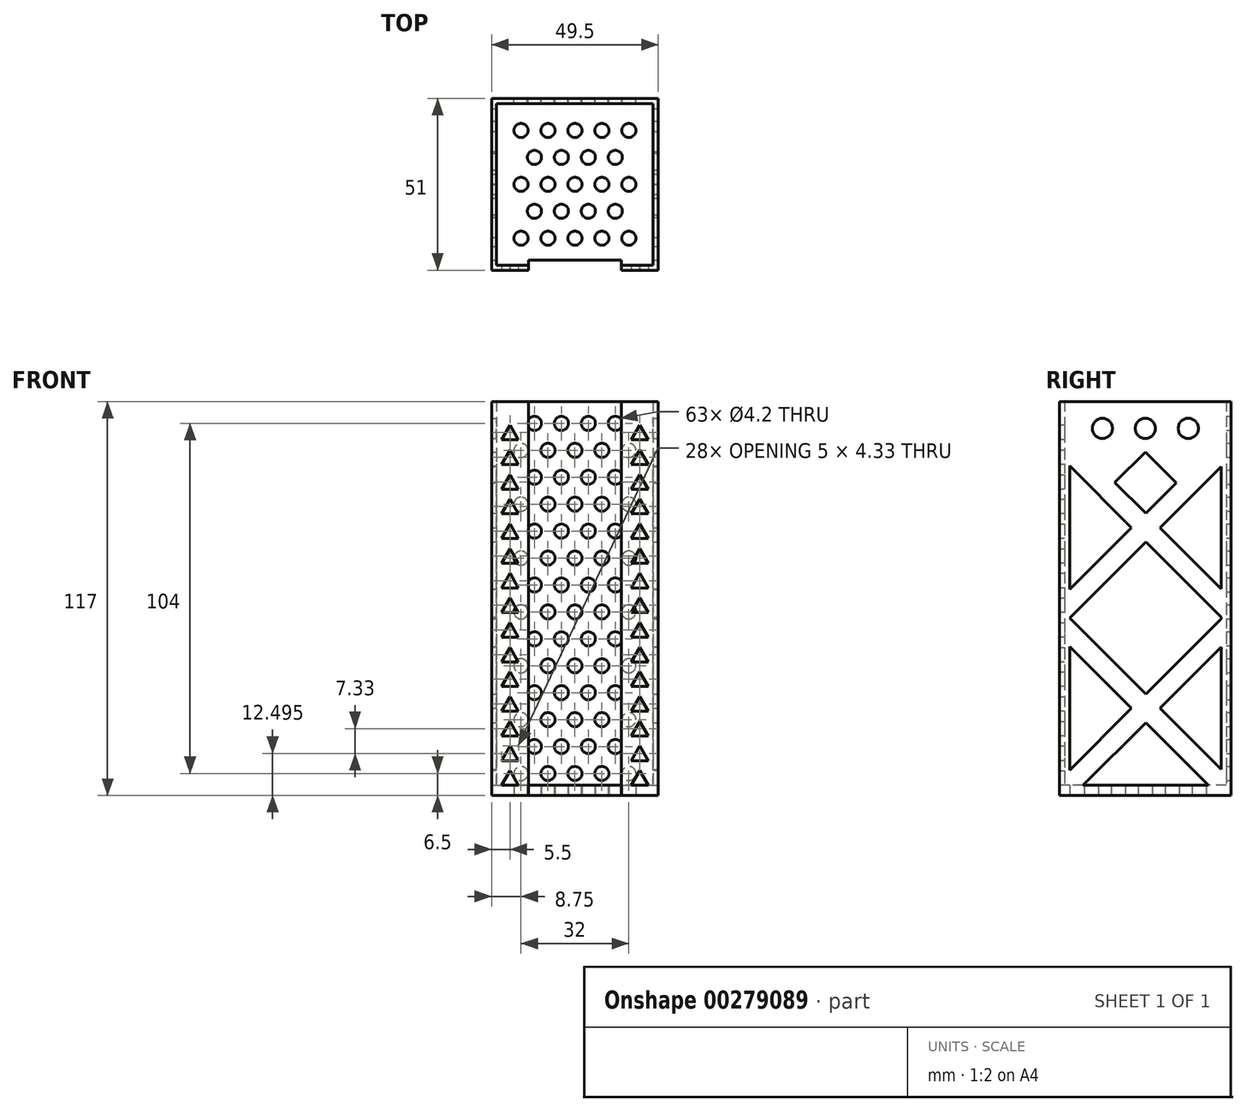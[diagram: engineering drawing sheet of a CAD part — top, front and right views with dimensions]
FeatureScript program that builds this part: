
annotation { "Feature Type Name" : "Feature", "Feature Type Description" : "" }
export const myFeature = defineFeature(function(context is Context, id is Id, definition is map)
    precondition{}
    {
        {
            var Q0;
            Q0=qCreatedBy(makeId("Top.planeOp"),FACE);
            var sketch = newSketch(context, id + "F0", { "sketchPlane" : qUnion([Q0])});
            skLineSegment(sketch, "E0.bottom", {"start": v(-24.75, 25.5) * mm, "end": v(24.75, 25.5) * mm});
            skLineSegment(sketch, "E0.top", {"start": v(-24.75, -25.5) * mm, "end": v(24.75, -25.5) * mm});
            skLineSegment(sketch, "E0.left", {"start": v(-24.75, 25.5) * mm, "end": v(-24.75, -25.5) * mm});
            skLineSegment(sketch, "E0.right", {"start": v(24.75, 25.5) * mm, "end": v(24.75, -25.5) * mm});
            skPoint(sketch, "E0.middle", {"position": v(0, 0) * mm});
            skSolve(sketch);
        }
        {
            var Q0;
            Q0=makeQuery(id+"F0.imprint","IMPRINT",FACE,{"disambiguationData":[TD([[makeQuery(id+"F0.imprint","IMPRINT",EDGE,{"derivedFrom":sQuery(id+"F0.wireOp",EDGE,"E0.bottom")}),-1.0]])]});
            extrude(context, id + "F1", {"entities" : qUnion([Q0]), "depth" : 3 * mm});
        }
        {
            var Q0;
            Q0=makeQuery(id+"F1.opExtrude","CAP_FACE",FACE,{"disambiguationData":[OSD([sQuery(id+"F0.wireOp",EDGE,"E0.bottom"),sQuery(id+"F0.wireOp",EDGE,"E0.top"),sQuery(id+"F0.wireOp",EDGE,"E0.left"),sQuery(id+"F0.wireOp",EDGE,"E0.right")])],"isStart":false});
            var sketch = newSketch(context, id + "F2", { "sketchPlane" : qUnion([Q0])});
            skLineSegment(sketch, "E1.bottom", {"start": v(-23.25, 24) * mm, "end": v(23.25, 24) * mm});
            skLineSegment(sketch, "E1.top", {"start": v(-23.25, -24) * mm, "end": v(23.25, -24) * mm});
            skLineSegment(sketch, "E1.left", {"start": v(-23.25, 24) * mm, "end": v(-23.25, -24) * mm});
            skLineSegment(sketch, "E1.right", {"start": v(23.25, 24) * mm, "end": v(23.25, -24) * mm});
            skPoint(sketch, "E1.middle", {"position": v(0, 0) * mm});
            skLineSegment(sketch, "E2.bottom", {"start": v(-24.75, 25.5) * mm, "end": v(24.75, 25.5) * mm});
            skLineSegment(sketch, "E2.top", {"start": v(-24.75, -25.5) * mm, "end": v(24.75, -25.5) * mm});
            skLineSegment(sketch, "E2.left", {"start": v(-24.75, 25.5) * mm, "end": v(-24.75, -25.5) * mm});
            skLineSegment(sketch, "E2.right", {"start": v(24.75, 25.5) * mm, "end": v(24.75, -25.5) * mm});
            skSolve(sketch);
        }
        {
            var Q0;
            Q0 = qSketchRegion(id + "F2", true);
            extrude(context, id + "F3", {"entities" : qUnion([Q0]), "operationType" : NewBodyOperationType.ADD, "depth" : 114 * mm});
        }
        {
            var Q0;
            Q0=makeQuery(id+"F3.boolean.opBoolean","MERGE",FACE,{"derivedFrom":[makeQuery(id+"F1.opExtrude","SWEPT_FACE",FACE,{"disambiguationData":[OSD([sQuery(id+"F0.wireOp",EDGE,"E0.top")])]}),makeQuery(id+"F3.opExtrude","SWEPT_FACE",FACE,{"disambiguationData":[OSD([sQuery(id+"F2.wireOp",EDGE,"E2.top")])]})]});
            var sketch = newSketch(context, id + "F4", { "sketchPlane" : qUnion([Q0])});
            skLineSegment(sketch, "E3.bottom", {"start": v(-24.75, 117) * mm, "end": v(-13.75, 117) * mm});
            skLineSegment(sketch, "E3.top", {"start": v(-24.75, 0) * mm, "end": v(-13.75, 0) * mm});
            skLineSegment(sketch, "E3.left", {"start": v(-24.75, 117) * mm, "end": v(-24.75, 0) * mm});
            skLineSegment(sketch, "E3.right", {"start": v(-13.75, 117) * mm, "end": v(-13.75, 0) * mm});
            skLineSegment(sketch, "E4.bottom", {"start": v(24.75, 117) * mm, "end": v(13.75, 117) * mm});
            skLineSegment(sketch, "E4.top", {"start": v(24.75, 0) * mm, "end": v(13.75, 0) * mm});
            skLineSegment(sketch, "E4.left", {"start": v(24.75, 117) * mm, "end": v(24.75, 0) * mm});
            skLineSegment(sketch, "E4.right", {"start": v(13.75, 117) * mm, "end": v(13.75, 0) * mm});
            skLineSegment(sketch, "E5.bottom", {"start": v(-13.75, 117) * mm, "end": v(13.75, 117) * mm});
            skLineSegment(sketch, "E5.top", {"start": v(-13.75, 0) * mm, "end": v(13.75, 0) * mm});
            skSolve(sketch);
        }
        {
            var Q0;
            Q0=makeQuery(id+"F4.imprint","IMPRINT",FACE,{"disambiguationData":[TD([[makeQuery(id+"F4.imprint","IMPRINT",EDGE,{"derivedFrom":sQuery(id+"F4.wireOp",EDGE,"E5.bottom")}),-1.0]])]});
            extrude(context, id + "F5", {"entities" : qUnion([Q0]), "operationType" : NewBodyOperationType.REMOVE, "oppositeDirection" : true, "depth" : 3 * mm});
        }
        {
            var Q0;
            Q0=makeQuery(id+"F3.boolean.opBoolean","MERGE",FACE,{"derivedFrom":[makeQuery(id+"F1.opExtrude","SWEPT_FACE",FACE,{"disambiguationData":[OSD([sQuery(id+"F0.wireOp",EDGE,"E0.bottom")])]}),makeQuery(id+"F3.opExtrude","SWEPT_FACE",FACE,{"disambiguationData":[OSD([sQuery(id+"F2.wireOp",EDGE,"E2.bottom")])]})]});
            var sketch = newSketch(context, id + "F6", { "sketchPlane" : qUnion([Q0])});
            skPoint(sketch, "E6.endSnap0", {"position": v(0, 0) * mm});
            skLineSegment(sketch, "E7", {"start": v(0, 6.5) * mm, "end": v(-8, 6.5) * mm});
            skLineSegment(sketch, "E8", {"start": v(-8, 6.5) * mm, "end": v(-16, 6.5) * mm});
            skLineSegment(sketch, "E9", {"start": v(0, 6.5) * mm, "end": v(8, 6.5) * mm});
            skLineSegment(sketch, "E10", {"start": v(8, 6.5) * mm, "end": v(16, 6.5) * mm});
            skCircle(sketch, "E11", {"center": v(-16, 6.5) * mm, "radius": 2.1 * mm});
            skCircle(sketch, "E12", {"center": v(-8, 6.5) * mm, "radius": 2.1 * mm});
            skCircle(sketch, "E13", {"center": v(0, 6.5) * mm, "radius": 2.1 * mm});
            skCircle(sketch, "E14", {"center": v(8, 6.5) * mm, "radius": 2.1 * mm});
            skCircle(sketch, "E15", {"center": v(16, 6.5) * mm, "radius": 2.1 * mm});
            skLineSegment(sketch, "E16", {"start": v(-12, 6.5) * mm, "end": v(-12, 14.5) * mm});
            skLineSegment(sketch, "E17", {"start": v(-4, 6.5) * mm, "end": v(-4, 14.5) * mm});
            skLineSegment(sketch, "E18", {"start": v(4, 6.5) * mm, "end": v(4, 14.5) * mm});
            skLineSegment(sketch, "E19", {"start": v(12, 6.5) * mm, "end": v(12, 14.5) * mm});
            skCircle(sketch, "E20", {"center": v(-12, 14.5) * mm, "radius": 2.1 * mm});
            skCircle(sketch, "E21", {"center": v(-4, 14.5) * mm, "radius": 2.1 * mm});
            skCircle(sketch, "E22", {"center": v(4, 14.5) * mm, "radius": 2.1 * mm});
            skCircle(sketch, "E23", {"center": v(12, 14.5) * mm, "radius": 2.1 * mm});
            skCircle(sketch, "E24.0.1.0", {"center": v(12, 30.5) * mm, "radius": 2.1 * mm});
            skLineSegment(sketch, "E24.0.1.1", {"start": v(12, 22.5) * mm, "end": v(12, 30.5) * mm});
            skCircle(sketch, "E24.0.1.2", {"center": v(-4, 30.5) * mm, "radius": 2.1 * mm});
            skCircle(sketch, "E24.0.1.3", {"center": v(-12, 30.5) * mm, "radius": 2.1 * mm});
            skLineSegment(sketch, "E24.0.1.4", {"start": v(0, 14.5) * mm, "end": v(0, 22.5) * mm});
            skPoint(sketch, "E24.0.1.5", {"position": v(0, 16) * mm});
            skLineSegment(sketch, "E24.0.1.6", {"start": v(-8, 22.5) * mm, "end": v(-16, 22.5) * mm});
            skLineSegment(sketch, "E24.0.1.7", {"start": v(0, 22.5) * mm, "end": v(8, 22.5) * mm});
            skCircle(sketch, "E24.0.1.8", {"center": v(-16, 22.5) * mm, "radius": 2.1 * mm});
            skCircle(sketch, "E24.0.1.9", {"center": v(-8, 22.5) * mm, "radius": 2.1 * mm});
            skCircle(sketch, "E24.0.1.10", {"center": v(0, 22.5) * mm, "radius": 2.1 * mm});
            skLineSegment(sketch, "E24.0.1.11", {"start": v(4, 22.5) * mm, "end": v(4, 30.5) * mm});
            skLineSegment(sketch, "E24.0.1.12", {"start": v(-4, 22.5) * mm, "end": v(-4, 30.5) * mm});
            skLineSegment(sketch, "E24.0.1.13", {"start": v(-12, 22.5) * mm, "end": v(-12, 30.5) * mm});
            skCircle(sketch, "E24.0.1.14", {"center": v(4, 30.5) * mm, "radius": 2.1 * mm});
            skCircle(sketch, "E24.0.1.15", {"center": v(16, 22.5) * mm, "radius": 2.1 * mm});
            skCircle(sketch, "E24.0.1.16", {"center": v(8, 22.5) * mm, "radius": 2.1 * mm});
            skLineSegment(sketch, "E24.0.1.17", {"start": v(0, 22.5) * mm, "end": v(-8, 22.5) * mm});
            skLineSegment(sketch, "E24.0.1.18", {"start": v(8, 22.5) * mm, "end": v(16, 22.5) * mm});
            skCircle(sketch, "E24.0.2.0", {"center": v(12, 46.5) * mm, "radius": 2.1 * mm});
            skLineSegment(sketch, "E24.0.2.1", {"start": v(12, 38.5) * mm, "end": v(12, 46.5) * mm});
            skCircle(sketch, "E24.0.2.2", {"center": v(-4, 46.5) * mm, "radius": 2.1 * mm});
            skCircle(sketch, "E24.0.2.3", {"center": v(-12, 46.5) * mm, "radius": 2.1 * mm});
            skLineSegment(sketch, "E24.0.2.4", {"start": v(0, 30.5) * mm, "end": v(0, 38.5) * mm});
            skPoint(sketch, "E24.0.2.5", {"position": v(0, 32) * mm});
            skLineSegment(sketch, "E24.0.2.6", {"start": v(-8, 38.5) * mm, "end": v(-16, 38.5) * mm});
            skLineSegment(sketch, "E24.0.2.7", {"start": v(0, 38.5) * mm, "end": v(8, 38.5) * mm});
            skCircle(sketch, "E24.0.2.8", {"center": v(-16, 38.5) * mm, "radius": 2.1 * mm});
            skCircle(sketch, "E24.0.2.9", {"center": v(-8, 38.5) * mm, "radius": 2.1 * mm});
            skCircle(sketch, "E24.0.2.10", {"center": v(0, 38.5) * mm, "radius": 2.1 * mm});
            skLineSegment(sketch, "E24.0.2.11", {"start": v(4, 38.5) * mm, "end": v(4, 46.5) * mm});
            skLineSegment(sketch, "E24.0.2.12", {"start": v(-4, 38.5) * mm, "end": v(-4, 46.5) * mm});
            skLineSegment(sketch, "E24.0.2.13", {"start": v(-12, 38.5) * mm, "end": v(-12, 46.5) * mm});
            skCircle(sketch, "E24.0.2.14", {"center": v(4, 46.5) * mm, "radius": 2.1 * mm});
            skCircle(sketch, "E24.0.2.15", {"center": v(16, 38.5) * mm, "radius": 2.1 * mm});
            skCircle(sketch, "E24.0.2.16", {"center": v(8, 38.5) * mm, "radius": 2.1 * mm});
            skLineSegment(sketch, "E24.0.2.17", {"start": v(0, 38.5) * mm, "end": v(-8, 38.5) * mm});
            skLineSegment(sketch, "E24.0.2.18", {"start": v(8, 38.5) * mm, "end": v(16, 38.5) * mm});
            skCircle(sketch, "E24.0.3.0", {"center": v(12, 62.5) * mm, "radius": 2.1 * mm});
            skLineSegment(sketch, "E24.0.3.1", {"start": v(12, 54.5) * mm, "end": v(12, 62.5) * mm});
            skCircle(sketch, "E24.0.3.2", {"center": v(-4, 62.5) * mm, "radius": 2.1 * mm});
            skCircle(sketch, "E24.0.3.3", {"center": v(-12, 62.5) * mm, "radius": 2.1 * mm});
            skLineSegment(sketch, "E24.0.3.4", {"start": v(0, 46.5) * mm, "end": v(0, 54.5) * mm});
            skPoint(sketch, "E24.0.3.5", {"position": v(0, 48) * mm});
            skLineSegment(sketch, "E24.0.3.6", {"start": v(-8, 54.5) * mm, "end": v(-16, 54.5) * mm});
            skLineSegment(sketch, "E24.0.3.7", {"start": v(0, 54.5) * mm, "end": v(8, 54.5) * mm});
            skCircle(sketch, "E24.0.3.8", {"center": v(-16, 54.5) * mm, "radius": 2.1 * mm});
            skCircle(sketch, "E24.0.3.9", {"center": v(-8, 54.5) * mm, "radius": 2.1 * mm});
            skCircle(sketch, "E24.0.3.10", {"center": v(0, 54.5) * mm, "radius": 2.1 * mm});
            skLineSegment(sketch, "E24.0.3.11", {"start": v(4, 54.5) * mm, "end": v(4, 62.5) * mm});
            skLineSegment(sketch, "E24.0.3.12", {"start": v(-4, 54.5) * mm, "end": v(-4, 62.5) * mm});
            skLineSegment(sketch, "E24.0.3.13", {"start": v(-12, 54.5) * mm, "end": v(-12, 62.5) * mm});
            skCircle(sketch, "E24.0.3.14", {"center": v(4, 62.5) * mm, "radius": 2.1 * mm});
            skCircle(sketch, "E24.0.3.15", {"center": v(16, 54.5) * mm, "radius": 2.1 * mm});
            skCircle(sketch, "E24.0.3.16", {"center": v(8, 54.5) * mm, "radius": 2.1 * mm});
            skLineSegment(sketch, "E24.0.3.17", {"start": v(0, 54.5) * mm, "end": v(-8, 54.5) * mm});
            skLineSegment(sketch, "E24.0.3.18", {"start": v(8, 54.5) * mm, "end": v(16, 54.5) * mm});
            skCircle(sketch, "E24.0.4.0", {"center": v(12, 78.5) * mm, "radius": 2.1 * mm});
            skLineSegment(sketch, "E24.0.4.1", {"start": v(12, 70.5) * mm, "end": v(12, 78.5) * mm});
            skCircle(sketch, "E24.0.4.2", {"center": v(-4, 78.5) * mm, "radius": 2.1 * mm});
            skCircle(sketch, "E24.0.4.3", {"center": v(-12, 78.5) * mm, "radius": 2.1 * mm});
            skLineSegment(sketch, "E24.0.4.4", {"start": v(0, 62.5) * mm, "end": v(0, 70.5) * mm});
            skPoint(sketch, "E24.0.4.5", {"position": v(0, 64) * mm});
            skLineSegment(sketch, "E24.0.4.6", {"start": v(-8, 70.5) * mm, "end": v(-16, 70.5) * mm});
            skLineSegment(sketch, "E24.0.4.7", {"start": v(0, 70.5) * mm, "end": v(8, 70.5) * mm});
            skCircle(sketch, "E24.0.4.8", {"center": v(-16, 70.5) * mm, "radius": 2.1 * mm});
            skCircle(sketch, "E24.0.4.9", {"center": v(-8, 70.5) * mm, "radius": 2.1 * mm});
            skCircle(sketch, "E24.0.4.10", {"center": v(0, 70.5) * mm, "radius": 2.1 * mm});
            skLineSegment(sketch, "E24.0.4.11", {"start": v(4, 70.5) * mm, "end": v(4, 78.5) * mm});
            skLineSegment(sketch, "E24.0.4.12", {"start": v(-4, 70.5) * mm, "end": v(-4, 78.5) * mm});
            skLineSegment(sketch, "E24.0.4.13", {"start": v(-12, 70.5) * mm, "end": v(-12, 78.5) * mm});
            skCircle(sketch, "E24.0.4.14", {"center": v(4, 78.5) * mm, "radius": 2.1 * mm});
            skCircle(sketch, "E24.0.4.15", {"center": v(16, 70.5) * mm, "radius": 2.1 * mm});
            skCircle(sketch, "E24.0.4.16", {"center": v(8, 70.5) * mm, "radius": 2.1 * mm});
            skLineSegment(sketch, "E24.0.4.17", {"start": v(0, 70.5) * mm, "end": v(-8, 70.5) * mm});
            skLineSegment(sketch, "E24.0.4.18", {"start": v(8, 70.5) * mm, "end": v(16, 70.5) * mm});
            skCircle(sketch, "E24.0.5.0", {"center": v(12, 94.5) * mm, "radius": 2.1 * mm});
            skLineSegment(sketch, "E24.0.5.1", {"start": v(12, 86.5) * mm, "end": v(12, 94.5) * mm});
            skCircle(sketch, "E24.0.5.2", {"center": v(-4, 94.5) * mm, "radius": 2.1 * mm});
            skCircle(sketch, "E24.0.5.3", {"center": v(-12, 94.5) * mm, "radius": 2.1 * mm});
            skLineSegment(sketch, "E24.0.5.4", {"start": v(0, 78.5) * mm, "end": v(0, 86.5) * mm});
            skPoint(sketch, "E24.0.5.5", {"position": v(0, 80) * mm});
            skLineSegment(sketch, "E24.0.5.6", {"start": v(-8, 86.5) * mm, "end": v(-16, 86.5) * mm});
            skLineSegment(sketch, "E24.0.5.7", {"start": v(0, 86.5) * mm, "end": v(8, 86.5) * mm});
            skCircle(sketch, "E24.0.5.8", {"center": v(-16, 86.5) * mm, "radius": 2.1 * mm});
            skCircle(sketch, "E24.0.5.9", {"center": v(-8, 86.5) * mm, "radius": 2.1 * mm});
            skCircle(sketch, "E24.0.5.10", {"center": v(0, 86.5) * mm, "radius": 2.1 * mm});
            skLineSegment(sketch, "E24.0.5.11", {"start": v(4, 86.5) * mm, "end": v(4, 94.5) * mm});
            skLineSegment(sketch, "E24.0.5.12", {"start": v(-4, 86.5) * mm, "end": v(-4, 94.5) * mm});
            skLineSegment(sketch, "E24.0.5.13", {"start": v(-12, 86.5) * mm, "end": v(-12, 94.5) * mm});
            skCircle(sketch, "E24.0.5.14", {"center": v(4, 94.5) * mm, "radius": 2.1 * mm});
            skCircle(sketch, "E24.0.5.15", {"center": v(16, 86.5) * mm, "radius": 2.1 * mm});
            skCircle(sketch, "E24.0.5.16", {"center": v(8, 86.5) * mm, "radius": 2.1 * mm});
            skLineSegment(sketch, "E24.0.5.17", {"start": v(0, 86.5) * mm, "end": v(-8, 86.5) * mm});
            skLineSegment(sketch, "E24.0.5.18", {"start": v(8, 86.5) * mm, "end": v(16, 86.5) * mm});
            skCircle(sketch, "E24.0.6.0", {"center": v(12, 110.5) * mm, "radius": 2.1 * mm});
            skLineSegment(sketch, "E24.0.6.1", {"start": v(12, 102.5) * mm, "end": v(12, 110.5) * mm});
            skCircle(sketch, "E24.0.6.2", {"center": v(-4, 110.5) * mm, "radius": 2.1 * mm});
            skCircle(sketch, "E24.0.6.3", {"center": v(-12, 110.5) * mm, "radius": 2.1 * mm});
            skLineSegment(sketch, "E24.0.6.4", {"start": v(0, 94.5) * mm, "end": v(0, 102.5) * mm});
            skPoint(sketch, "E24.0.6.5", {"position": v(0, 96) * mm});
            skLineSegment(sketch, "E24.0.6.6", {"start": v(-8, 102.5) * mm, "end": v(-16, 102.5) * mm});
            skLineSegment(sketch, "E24.0.6.7", {"start": v(0, 102.5) * mm, "end": v(8, 102.5) * mm});
            skCircle(sketch, "E24.0.6.8", {"center": v(-16, 102.5) * mm, "radius": 2.1 * mm});
            skCircle(sketch, "E24.0.6.9", {"center": v(-8, 102.5) * mm, "radius": 2.1 * mm});
            skCircle(sketch, "E24.0.6.10", {"center": v(0, 102.5) * mm, "radius": 2.1 * mm});
            skLineSegment(sketch, "E24.0.6.11", {"start": v(4, 102.5) * mm, "end": v(4, 110.5) * mm});
            skLineSegment(sketch, "E24.0.6.12", {"start": v(-4, 102.5) * mm, "end": v(-4, 110.5) * mm});
            skLineSegment(sketch, "E24.0.6.13", {"start": v(-12, 102.5) * mm, "end": v(-12, 110.5) * mm});
            skCircle(sketch, "E24.0.6.14", {"center": v(4, 110.5) * mm, "radius": 2.1 * mm});
            skCircle(sketch, "E24.0.6.15", {"center": v(16, 102.5) * mm, "radius": 2.1 * mm});
            skCircle(sketch, "E24.0.6.16", {"center": v(8, 102.5) * mm, "radius": 2.1 * mm});
            skLineSegment(sketch, "E24.0.6.17", {"start": v(0, 102.5) * mm, "end": v(-8, 102.5) * mm});
            skLineSegment(sketch, "E24.0.6.18", {"start": v(8, 102.5) * mm, "end": v(16, 102.5) * mm});
            skLineSegment(sketch, "E24.direction1", {"start": v(-16, 6.5) * mm, "end": v(9, 6.5) * mm, "construction": true});
            skLineSegment(sketch, "E24.direction2", {"start": v(-16, 6.5) * mm, "end": v(-16, 22.5) * mm, "construction": true});
            skLineSegment(sketch, "E25", {"start": v(0, 6.5) * mm, "end": v(0, 0) * mm});
            skLineSegment(sketch, "E26", {"start": v(-4, 110.5) * mm, "end": v(4, 110.5) * mm});
            skLineSegment(sketch, "E27", {"start": v(0, 110.5) * mm, "end": v(0, 117) * mm});
            skSolve(sketch);
        }
        {
            var Q0;
            Q0=makeQuery(id+"F6.imprint","IMPRINT",FACE,{"disambiguationData":[TD([[makeQuery(id+"F6.imprint","IMPRINT",EDGE,{"derivedFrom":sQuery(id+"F6.wireOp",EDGE,"E11")}),1.0]])]});
            var Q1;
            Q1=makeQuery(id+"F6.imprint","IMPRINT",FACE,{"disambiguationData":[TD([[makeQuery(id+"F6.imprint","IMPRINT",EDGE,{"derivedFrom":sQuery(id+"F6.wireOp",EDGE,"E15")}),1.0]])]});
            var Q2;
            Q2=makeQuery(id+"F6.imprint","IMPRINT",FACE,{"disambiguationData":[TD([[makeQuery(id+"F6.imprint","IMPRINT",EDGE,{"derivedFrom":sQuery(id+"F6.wireOp",EDGE,"E20")}),1.0]])]});
            var Q3;
            Q3=makeQuery(id+"F6.imprint","IMPRINT",FACE,{"disambiguationData":[TD([[makeQuery(id+"F6.imprint","IMPRINT",EDGE,{"derivedFrom":sQuery(id+"F6.wireOp",EDGE,"E21")}),1.0]])]});
            var Q4;
            Q4=makeQuery(id+"F6.imprint","IMPRINT",FACE,{"disambiguationData":[TD([[makeQuery(id+"F6.imprint","IMPRINT",EDGE,{"derivedFrom":sQuery(id+"F6.wireOp",EDGE,"E22")}),1.0]])]});
            var Q5;
            Q5=makeQuery(id+"F6.imprint","IMPRINT",FACE,{"disambiguationData":[TD([[makeQuery(id+"F6.imprint","IMPRINT",EDGE,{"derivedFrom":sQuery(id+"F6.wireOp",EDGE,"E23")}),1.0]])]});
            var Q6;
            Q6=makeQuery(id+"F6.imprint","IMPRINT",FACE,{"disambiguationData":[TD([[makeQuery(id+"F6.imprint","IMPRINT",EDGE,{"derivedFrom":sQuery(id+"F6.wireOp",EDGE,"E24.0.1.0")}),1.0]])]});
            var Q7;
            Q7=makeQuery(id+"F6.imprint","IMPRINT",FACE,{"disambiguationData":[TD([[makeQuery(id+"F6.imprint","IMPRINT",EDGE,{"derivedFrom":sQuery(id+"F6.wireOp",EDGE,"E24.0.1.2")}),1.0]])]});
            var Q8;
            Q8=makeQuery(id+"F6.imprint","IMPRINT",FACE,{"disambiguationData":[TD([[makeQuery(id+"F6.imprint","IMPRINT",EDGE,{"derivedFrom":sQuery(id+"F6.wireOp",EDGE,"E24.0.1.3")}),1.0]])]});
            var Q9;
            Q9=makeQuery(id+"F6.imprint","IMPRINT",FACE,{"disambiguationData":[TD([[makeQuery(id+"F6.imprint","IMPRINT",EDGE,{"derivedFrom":sQuery(id+"F6.wireOp",EDGE,"E24.0.1.8")}),1.0]])]});
            var Q10;
            Q10=makeQuery(id+"F6.imprint","IMPRINT",FACE,{"disambiguationData":[TD([[makeQuery(id+"F6.imprint","IMPRINT",EDGE,{"derivedFrom":sQuery(id+"F6.wireOp",EDGE,"E24.0.1.14")}),1.0]])]});
            var Q11;
            Q11=makeQuery(id+"F6.imprint","IMPRINT",FACE,{"disambiguationData":[TD([[makeQuery(id+"F6.imprint","IMPRINT",EDGE,{"derivedFrom":sQuery(id+"F6.wireOp",EDGE,"E24.0.1.15")}),1.0]])]});
            var Q12;
            Q12=makeQuery(id+"F6.imprint","IMPRINT",FACE,{"disambiguationData":[TD([[makeQuery(id+"F6.imprint","IMPRINT",EDGE,{"derivedFrom":sQuery(id+"F6.wireOp",EDGE,"E24.0.2.0")}),1.0]])]});
            var Q13;
            Q13=makeQuery(id+"F6.imprint","IMPRINT",FACE,{"disambiguationData":[TD([[makeQuery(id+"F6.imprint","IMPRINT",EDGE,{"derivedFrom":sQuery(id+"F6.wireOp",EDGE,"E24.0.2.2")}),1.0]])]});
            var Q14;
            Q14=makeQuery(id+"F6.imprint","IMPRINT",FACE,{"disambiguationData":[TD([[makeQuery(id+"F6.imprint","IMPRINT",EDGE,{"derivedFrom":sQuery(id+"F6.wireOp",EDGE,"E24.0.2.3")}),1.0]])]});
            var Q15;
            Q15=makeQuery(id+"F6.imprint","IMPRINT",FACE,{"disambiguationData":[TD([[makeQuery(id+"F6.imprint","IMPRINT",EDGE,{"derivedFrom":sQuery(id+"F6.wireOp",EDGE,"E24.0.2.8")}),1.0]])]});
            var Q16;
            Q16=makeQuery(id+"F6.imprint","IMPRINT",FACE,{"disambiguationData":[TD([[makeQuery(id+"F6.imprint","IMPRINT",EDGE,{"derivedFrom":sQuery(id+"F6.wireOp",EDGE,"E24.0.2.14")}),1.0]])]});
            var Q17;
            Q17=makeQuery(id+"F6.imprint","IMPRINT",FACE,{"disambiguationData":[TD([[makeQuery(id+"F6.imprint","IMPRINT",EDGE,{"derivedFrom":sQuery(id+"F6.wireOp",EDGE,"E24.0.2.15")}),1.0]])]});
            var Q18;
            Q18=makeQuery(id+"F6.imprint","IMPRINT",FACE,{"disambiguationData":[TD([[makeQuery(id+"F6.imprint","IMPRINT",EDGE,{"derivedFrom":sQuery(id+"F6.wireOp",EDGE,"E24.0.3.0")}),1.0]])]});
            var Q19;
            Q19=makeQuery(id+"F6.imprint","IMPRINT",FACE,{"disambiguationData":[TD([[makeQuery(id+"F6.imprint","IMPRINT",EDGE,{"derivedFrom":sQuery(id+"F6.wireOp",EDGE,"E24.0.3.2")}),1.0]])]});
            var Q20;
            Q20=makeQuery(id+"F6.imprint","IMPRINT",FACE,{"disambiguationData":[TD([[makeQuery(id+"F6.imprint","IMPRINT",EDGE,{"derivedFrom":sQuery(id+"F6.wireOp",EDGE,"E24.0.3.3")}),1.0]])]});
            var Q21;
            Q21=makeQuery(id+"F6.imprint","IMPRINT",FACE,{"disambiguationData":[TD([[makeQuery(id+"F6.imprint","IMPRINT",EDGE,{"derivedFrom":sQuery(id+"F6.wireOp",EDGE,"E24.0.3.8")}),1.0]])]});
            var Q22;
            Q22=makeQuery(id+"F6.imprint","IMPRINT",FACE,{"disambiguationData":[TD([[makeQuery(id+"F6.imprint","IMPRINT",EDGE,{"derivedFrom":sQuery(id+"F6.wireOp",EDGE,"E24.0.3.14")}),1.0]])]});
            var Q23;
            Q23=makeQuery(id+"F6.imprint","IMPRINT",FACE,{"disambiguationData":[TD([[makeQuery(id+"F6.imprint","IMPRINT",EDGE,{"derivedFrom":sQuery(id+"F6.wireOp",EDGE,"E24.0.3.15")}),1.0]])]});
            var Q24;
            Q24=makeQuery(id+"F6.imprint","IMPRINT",FACE,{"disambiguationData":[TD([[makeQuery(id+"F6.imprint","IMPRINT",EDGE,{"derivedFrom":sQuery(id+"F6.wireOp",EDGE,"E24.0.4.0")}),1.0]])]});
            var Q25;
            Q25=makeQuery(id+"F6.imprint","IMPRINT",FACE,{"disambiguationData":[TD([[makeQuery(id+"F6.imprint","IMPRINT",EDGE,{"derivedFrom":sQuery(id+"F6.wireOp",EDGE,"E24.0.4.2")}),1.0]])]});
            var Q26;
            Q26=makeQuery(id+"F6.imprint","IMPRINT",FACE,{"disambiguationData":[TD([[makeQuery(id+"F6.imprint","IMPRINT",EDGE,{"derivedFrom":sQuery(id+"F6.wireOp",EDGE,"E24.0.4.3")}),1.0]])]});
            var Q27;
            Q27=makeQuery(id+"F6.imprint","IMPRINT",FACE,{"disambiguationData":[TD([[makeQuery(id+"F6.imprint","IMPRINT",EDGE,{"derivedFrom":sQuery(id+"F6.wireOp",EDGE,"E24.0.4.8")}),1.0]])]});
            var Q28;
            Q28=makeQuery(id+"F6.imprint","IMPRINT",FACE,{"disambiguationData":[TD([[makeQuery(id+"F6.imprint","IMPRINT",EDGE,{"derivedFrom":sQuery(id+"F6.wireOp",EDGE,"E24.0.4.14")}),1.0]])]});
            var Q29;
            Q29=makeQuery(id+"F6.imprint","IMPRINT",FACE,{"disambiguationData":[TD([[makeQuery(id+"F6.imprint","IMPRINT",EDGE,{"derivedFrom":sQuery(id+"F6.wireOp",EDGE,"E24.0.4.15")}),1.0]])]});
            var Q30;
            Q30=makeQuery(id+"F6.imprint","IMPRINT",FACE,{"disambiguationData":[TD([[makeQuery(id+"F6.imprint","IMPRINT",EDGE,{"derivedFrom":sQuery(id+"F6.wireOp",EDGE,"E24.0.5.0")}),1.0]])]});
            var Q31;
            Q31=makeQuery(id+"F6.imprint","IMPRINT",FACE,{"disambiguationData":[TD([[makeQuery(id+"F6.imprint","IMPRINT",EDGE,{"derivedFrom":sQuery(id+"F6.wireOp",EDGE,"E24.0.5.2")}),1.0]])]});
            var Q32;
            Q32=makeQuery(id+"F6.imprint","IMPRINT",FACE,{"disambiguationData":[TD([[makeQuery(id+"F6.imprint","IMPRINT",EDGE,{"derivedFrom":sQuery(id+"F6.wireOp",EDGE,"E24.0.5.3")}),1.0]])]});
            var Q33;
            Q33=makeQuery(id+"F6.imprint","IMPRINT",FACE,{"disambiguationData":[TD([[makeQuery(id+"F6.imprint","IMPRINT",EDGE,{"derivedFrom":sQuery(id+"F6.wireOp",EDGE,"E24.0.5.8")}),1.0]])]});
            var Q34;
            Q34=makeQuery(id+"F6.imprint","IMPRINT",FACE,{"disambiguationData":[TD([[makeQuery(id+"F6.imprint","IMPRINT",EDGE,{"derivedFrom":sQuery(id+"F6.wireOp",EDGE,"E24.0.5.14")}),1.0]])]});
            var Q35;
            Q35=makeQuery(id+"F6.imprint","IMPRINT",FACE,{"disambiguationData":[TD([[makeQuery(id+"F6.imprint","IMPRINT",EDGE,{"derivedFrom":sQuery(id+"F6.wireOp",EDGE,"E24.0.5.15")}),1.0]])]});
            var Q36;
            Q36=makeQuery(id+"F6.imprint","IMPRINT",FACE,{"disambiguationData":[TD([[makeQuery(id+"F6.imprint","IMPRINT",EDGE,{"derivedFrom":sQuery(id+"F6.wireOp",EDGE,"E24.0.6.0")}),1.0]])]});
            var Q37;
            Q37=makeQuery(id+"F6.imprint","IMPRINT",FACE,{"disambiguationData":[TD([[makeQuery(id+"F6.imprint","IMPRINT",EDGE,{"derivedFrom":sQuery(id+"F6.wireOp",EDGE,"E24.0.6.3")}),1.0]])]});
            var Q38;
            Q38=makeQuery(id+"F6.imprint","IMPRINT",FACE,{"disambiguationData":[TD([[makeQuery(id+"F6.imprint","IMPRINT",EDGE,{"derivedFrom":sQuery(id+"F6.wireOp",EDGE,"E24.0.6.8")}),1.0]])]});
            var Q39;
            Q39=makeQuery(id+"F6.imprint","IMPRINT",FACE,{"disambiguationData":[TD([[makeQuery(id+"F6.imprint","IMPRINT",EDGE,{"derivedFrom":sQuery(id+"F6.wireOp",EDGE,"E24.0.6.15")}),1.0]])]});
            var Q40;
            {var subQ0=sQuery(id+"F6.wireOp",EDGE,"E8");var subQ1=sQuery(id+"F6.wireOp",EDGE,"E7");var subQ2=makeQuery(id+"F6.imprint","INTERSECT",VERTEX,{"derivedFrom":[subQ1,subQ0]});Q40=makeQuery(id+"F6.imprint","IMPRINT",FACE,{"disambiguationData":[TD([[makeQuery(id+"F6.imprint","IMPRINT",EDGE,{"disambiguationData":[TD([[subQ2,1.0]])],"derivedFrom":subQ1}),-1.0]])]});}
            var Q41;
            {var subQ0=sQuery(id+"F6.wireOp",EDGE,"E8");var subQ1=sQuery(id+"F6.wireOp",EDGE,"E7");var subQ2=makeQuery(id+"F6.imprint","INTERSECT",VERTEX,{"derivedFrom":[subQ1,subQ0]});Q41=makeQuery(id+"F6.imprint","IMPRINT",FACE,{"disambiguationData":[TD([[makeQuery(id+"F6.imprint","IMPRINT",EDGE,{"disambiguationData":[TD([[subQ2,1.0]])],"derivedFrom":subQ1}),1.0]])]});}
            var Q42;
            {var subQ0=sQuery(id+"F6.wireOp",EDGE,"E10");var subQ1=sQuery(id+"F6.wireOp",EDGE,"E9");var subQ2=makeQuery(id+"F6.imprint","INTERSECT",VERTEX,{"derivedFrom":[subQ1,subQ0]});Q42=makeQuery(id+"F6.imprint","IMPRINT",FACE,{"disambiguationData":[TD([[makeQuery(id+"F6.imprint","IMPRINT",EDGE,{"disambiguationData":[TD([[subQ2,1.0]])],"derivedFrom":subQ1}),1.0]])]});}
            var Q43;
            {var subQ0=sQuery(id+"F6.wireOp",EDGE,"E10");var subQ1=sQuery(id+"F6.wireOp",EDGE,"E9");var subQ2=makeQuery(id+"F6.imprint","INTERSECT",VERTEX,{"derivedFrom":[subQ1,subQ0]});Q43=makeQuery(id+"F6.imprint","IMPRINT",FACE,{"disambiguationData":[TD([[makeQuery(id+"F6.imprint","IMPRINT",EDGE,{"disambiguationData":[TD([[subQ2,1.0]])],"derivedFrom":subQ1}),-1.0]])]});}
            var Q44;
            {var subQ0=sQuery(id+"F6.wireOp",EDGE,"E24.0.1.17");var subQ1=sQuery(id+"F6.wireOp",EDGE,"E24.0.1.6");var subQ2=makeQuery(id+"F6.imprint","INTERSECT",VERTEX,{"derivedFrom":[subQ1,subQ0]});Q44=makeQuery(id+"F6.imprint","IMPRINT",FACE,{"disambiguationData":[TD([[makeQuery(id+"F6.imprint","IMPRINT",EDGE,{"disambiguationData":[TD([[subQ2,-1.0]])],"derivedFrom":subQ1}),-1.0]])]});}
            var Q45;
            {var subQ0=sQuery(id+"F6.wireOp",EDGE,"E24.0.1.17");var subQ1=sQuery(id+"F6.wireOp",EDGE,"E24.0.1.6");var subQ2=makeQuery(id+"F6.imprint","INTERSECT",VERTEX,{"derivedFrom":[subQ1,subQ0]});Q45=makeQuery(id+"F6.imprint","IMPRINT",FACE,{"disambiguationData":[TD([[makeQuery(id+"F6.imprint","IMPRINT",EDGE,{"disambiguationData":[TD([[subQ2,-1.0]])],"derivedFrom":subQ1}),1.0]])]});}
            var Q46;
            {var subQ0=sQuery(id+"F6.wireOp",EDGE,"E24.0.1.18");var subQ1=sQuery(id+"F6.wireOp",EDGE,"E24.0.1.7");var subQ2=makeQuery(id+"F6.imprint","INTERSECT",VERTEX,{"derivedFrom":[subQ1,subQ0]});Q46=makeQuery(id+"F6.imprint","IMPRINT",FACE,{"disambiguationData":[TD([[makeQuery(id+"F6.imprint","IMPRINT",EDGE,{"disambiguationData":[TD([[subQ2,1.0]])],"derivedFrom":subQ1}),1.0]])]});}
            var Q47;
            {var subQ0=sQuery(id+"F6.wireOp",EDGE,"E24.0.1.18");var subQ1=sQuery(id+"F6.wireOp",EDGE,"E24.0.1.7");var subQ2=makeQuery(id+"F6.imprint","INTERSECT",VERTEX,{"derivedFrom":[subQ1,subQ0]});Q47=makeQuery(id+"F6.imprint","IMPRINT",FACE,{"disambiguationData":[TD([[makeQuery(id+"F6.imprint","IMPRINT",EDGE,{"disambiguationData":[TD([[subQ2,1.0]])],"derivedFrom":subQ1}),-1.0]])]});}
            var Q48;
            {var subQ0=sQuery(id+"F6.wireOp",EDGE,"E24.0.2.17");var subQ1=sQuery(id+"F6.wireOp",EDGE,"E24.0.2.6");var subQ2=makeQuery(id+"F6.imprint","INTERSECT",VERTEX,{"derivedFrom":[subQ1,subQ0]});Q48=makeQuery(id+"F6.imprint","IMPRINT",FACE,{"disambiguationData":[TD([[makeQuery(id+"F6.imprint","IMPRINT",EDGE,{"disambiguationData":[TD([[subQ2,-1.0]])],"derivedFrom":subQ1}),-1.0]])]});}
            var Q49;
            {var subQ0=sQuery(id+"F6.wireOp",EDGE,"E24.0.2.17");var subQ1=sQuery(id+"F6.wireOp",EDGE,"E24.0.2.6");var subQ2=makeQuery(id+"F6.imprint","INTERSECT",VERTEX,{"derivedFrom":[subQ1,subQ0]});Q49=makeQuery(id+"F6.imprint","IMPRINT",FACE,{"disambiguationData":[TD([[makeQuery(id+"F6.imprint","IMPRINT",EDGE,{"disambiguationData":[TD([[subQ2,-1.0]])],"derivedFrom":subQ1}),1.0]])]});}
            var Q50;
            {var subQ0=sQuery(id+"F6.wireOp",EDGE,"E24.0.2.18");var subQ1=sQuery(id+"F6.wireOp",EDGE,"E24.0.2.7");var subQ2=makeQuery(id+"F6.imprint","INTERSECT",VERTEX,{"derivedFrom":[subQ1,subQ0]});Q50=makeQuery(id+"F6.imprint","IMPRINT",FACE,{"disambiguationData":[TD([[makeQuery(id+"F6.imprint","IMPRINT",EDGE,{"disambiguationData":[TD([[subQ2,1.0]])],"derivedFrom":subQ1}),1.0]])]});}
            var Q51;
            {var subQ0=sQuery(id+"F6.wireOp",EDGE,"E24.0.2.18");var subQ1=sQuery(id+"F6.wireOp",EDGE,"E24.0.2.7");var subQ2=makeQuery(id+"F6.imprint","INTERSECT",VERTEX,{"derivedFrom":[subQ1,subQ0]});Q51=makeQuery(id+"F6.imprint","IMPRINT",FACE,{"disambiguationData":[TD([[makeQuery(id+"F6.imprint","IMPRINT",EDGE,{"disambiguationData":[TD([[subQ2,1.0]])],"derivedFrom":subQ1}),-1.0]])]});}
            var Q52;
            {var subQ0=sQuery(id+"F6.wireOp",EDGE,"E24.0.3.17");var subQ1=sQuery(id+"F6.wireOp",EDGE,"E24.0.3.6");var subQ2=makeQuery(id+"F6.imprint","INTERSECT",VERTEX,{"derivedFrom":[subQ1,subQ0]});Q52=makeQuery(id+"F6.imprint","IMPRINT",FACE,{"disambiguationData":[TD([[makeQuery(id+"F6.imprint","IMPRINT",EDGE,{"disambiguationData":[TD([[subQ2,-1.0]])],"derivedFrom":subQ1}),-1.0]])]});}
            var Q53;
            {var subQ0=sQuery(id+"F6.wireOp",EDGE,"E24.0.3.17");var subQ1=sQuery(id+"F6.wireOp",EDGE,"E24.0.3.6");var subQ2=makeQuery(id+"F6.imprint","INTERSECT",VERTEX,{"derivedFrom":[subQ1,subQ0]});Q53=makeQuery(id+"F6.imprint","IMPRINT",FACE,{"disambiguationData":[TD([[makeQuery(id+"F6.imprint","IMPRINT",EDGE,{"disambiguationData":[TD([[subQ2,-1.0]])],"derivedFrom":subQ1}),1.0]])]});}
            var Q54;
            {var subQ0=sQuery(id+"F6.wireOp",EDGE,"E24.0.3.18");var subQ1=sQuery(id+"F6.wireOp",EDGE,"E24.0.3.7");var subQ2=makeQuery(id+"F6.imprint","INTERSECT",VERTEX,{"derivedFrom":[subQ1,subQ0]});Q54=makeQuery(id+"F6.imprint","IMPRINT",FACE,{"disambiguationData":[TD([[makeQuery(id+"F6.imprint","IMPRINT",EDGE,{"disambiguationData":[TD([[subQ2,1.0]])],"derivedFrom":subQ1}),1.0]])]});}
            var Q55;
            {var subQ0=sQuery(id+"F6.wireOp",EDGE,"E24.0.3.18");var subQ1=sQuery(id+"F6.wireOp",EDGE,"E24.0.3.7");var subQ2=makeQuery(id+"F6.imprint","INTERSECT",VERTEX,{"derivedFrom":[subQ1,subQ0]});Q55=makeQuery(id+"F6.imprint","IMPRINT",FACE,{"disambiguationData":[TD([[makeQuery(id+"F6.imprint","IMPRINT",EDGE,{"disambiguationData":[TD([[subQ2,1.0]])],"derivedFrom":subQ1}),-1.0]])]});}
            var Q56;
            {var subQ0=sQuery(id+"F6.wireOp",EDGE,"E24.0.4.17");var subQ1=sQuery(id+"F6.wireOp",EDGE,"E24.0.4.6");var subQ2=makeQuery(id+"F6.imprint","INTERSECT",VERTEX,{"derivedFrom":[subQ1,subQ0]});Q56=makeQuery(id+"F6.imprint","IMPRINT",FACE,{"disambiguationData":[TD([[makeQuery(id+"F6.imprint","IMPRINT",EDGE,{"disambiguationData":[TD([[subQ2,-1.0]])],"derivedFrom":subQ1}),-1.0]])]});}
            var Q57;
            {var subQ0=sQuery(id+"F6.wireOp",EDGE,"E24.0.4.17");var subQ1=sQuery(id+"F6.wireOp",EDGE,"E24.0.4.6");var subQ2=makeQuery(id+"F6.imprint","INTERSECT",VERTEX,{"derivedFrom":[subQ1,subQ0]});Q57=makeQuery(id+"F6.imprint","IMPRINT",FACE,{"disambiguationData":[TD([[makeQuery(id+"F6.imprint","IMPRINT",EDGE,{"disambiguationData":[TD([[subQ2,-1.0]])],"derivedFrom":subQ1}),1.0]])]});}
            var Q58;
            {var subQ0=sQuery(id+"F6.wireOp",EDGE,"E24.0.4.18");var subQ1=sQuery(id+"F6.wireOp",EDGE,"E24.0.4.7");var subQ2=makeQuery(id+"F6.imprint","INTERSECT",VERTEX,{"derivedFrom":[subQ1,subQ0]});Q58=makeQuery(id+"F6.imprint","IMPRINT",FACE,{"disambiguationData":[TD([[makeQuery(id+"F6.imprint","IMPRINT",EDGE,{"disambiguationData":[TD([[subQ2,1.0]])],"derivedFrom":subQ1}),1.0]])]});}
            var Q59;
            {var subQ0=sQuery(id+"F6.wireOp",EDGE,"E24.0.4.18");var subQ1=sQuery(id+"F6.wireOp",EDGE,"E24.0.4.7");var subQ2=makeQuery(id+"F6.imprint","INTERSECT",VERTEX,{"derivedFrom":[subQ1,subQ0]});Q59=makeQuery(id+"F6.imprint","IMPRINT",FACE,{"disambiguationData":[TD([[makeQuery(id+"F6.imprint","IMPRINT",EDGE,{"disambiguationData":[TD([[subQ2,1.0]])],"derivedFrom":subQ1}),-1.0]])]});}
            var Q60;
            {var subQ0=sQuery(id+"F6.wireOp",EDGE,"E24.0.5.17");var subQ1=sQuery(id+"F6.wireOp",EDGE,"E24.0.5.6");var subQ2=makeQuery(id+"F6.imprint","INTERSECT",VERTEX,{"derivedFrom":[subQ1,subQ0]});Q60=makeQuery(id+"F6.imprint","IMPRINT",FACE,{"disambiguationData":[TD([[makeQuery(id+"F6.imprint","IMPRINT",EDGE,{"disambiguationData":[TD([[subQ2,-1.0]])],"derivedFrom":subQ1}),-1.0]])]});}
            var Q61;
            {var subQ0=sQuery(id+"F6.wireOp",EDGE,"E24.0.5.17");var subQ1=sQuery(id+"F6.wireOp",EDGE,"E24.0.5.6");var subQ2=makeQuery(id+"F6.imprint","INTERSECT",VERTEX,{"derivedFrom":[subQ1,subQ0]});Q61=makeQuery(id+"F6.imprint","IMPRINT",FACE,{"disambiguationData":[TD([[makeQuery(id+"F6.imprint","IMPRINT",EDGE,{"disambiguationData":[TD([[subQ2,-1.0]])],"derivedFrom":subQ1}),1.0]])]});}
            var Q62;
            {var subQ0=sQuery(id+"F6.wireOp",EDGE,"E24.0.5.18");var subQ1=sQuery(id+"F6.wireOp",EDGE,"E24.0.5.7");var subQ2=makeQuery(id+"F6.imprint","INTERSECT",VERTEX,{"derivedFrom":[subQ1,subQ0]});Q62=makeQuery(id+"F6.imprint","IMPRINT",FACE,{"disambiguationData":[TD([[makeQuery(id+"F6.imprint","IMPRINT",EDGE,{"disambiguationData":[TD([[subQ2,1.0]])],"derivedFrom":subQ1}),1.0]])]});}
            var Q63;
            {var subQ0=sQuery(id+"F6.wireOp",EDGE,"E24.0.5.18");var subQ1=sQuery(id+"F6.wireOp",EDGE,"E24.0.5.7");var subQ2=makeQuery(id+"F6.imprint","INTERSECT",VERTEX,{"derivedFrom":[subQ1,subQ0]});Q63=makeQuery(id+"F6.imprint","IMPRINT",FACE,{"disambiguationData":[TD([[makeQuery(id+"F6.imprint","IMPRINT",EDGE,{"disambiguationData":[TD([[subQ2,1.0]])],"derivedFrom":subQ1}),-1.0]])]});}
            var Q64;
            {var subQ0=sQuery(id+"F6.wireOp",EDGE,"E24.0.6.12");var subQ1=sQuery(id+"F6.wireOp",EDGE,"E24.0.6.2");var subQ2=makeQuery(id+"F6.imprint","INTERSECT",VERTEX,{"derivedFrom":[subQ1,subQ0]});Q64=makeQuery(id+"F6.imprint","IMPRINT",FACE,{"disambiguationData":[TD([[makeQuery(id+"F6.imprint","IMPRINT",EDGE,{"disambiguationData":[TD([[subQ2,1.0]])],"derivedFrom":subQ1}),1.0]])]});}
            var Q65;
            {var subQ0=sQuery(id+"F6.wireOp",EDGE,"E24.0.6.12");var subQ1=sQuery(id+"F6.wireOp",EDGE,"E24.0.6.2");var subQ2=makeQuery(id+"F6.imprint","INTERSECT",VERTEX,{"derivedFrom":[subQ1,subQ0]});Q65=makeQuery(id+"F6.imprint","IMPRINT",FACE,{"disambiguationData":[TD([[makeQuery(id+"F6.imprint","IMPRINT",EDGE,{"disambiguationData":[TD([[subQ2,-1.0]])],"derivedFrom":subQ1}),1.0]])]});}
            var Q66;
            {var subQ0=sQuery(id+"F6.wireOp",EDGE,"E24.0.6.17");var subQ1=sQuery(id+"F6.wireOp",EDGE,"E24.0.6.6");var subQ2=makeQuery(id+"F6.imprint","INTERSECT",VERTEX,{"derivedFrom":[subQ1,subQ0]});Q66=makeQuery(id+"F6.imprint","IMPRINT",FACE,{"disambiguationData":[TD([[makeQuery(id+"F6.imprint","IMPRINT",EDGE,{"disambiguationData":[TD([[subQ2,-1.0]])],"derivedFrom":subQ1}),-1.0]])]});}
            var Q67;
            {var subQ0=sQuery(id+"F6.wireOp",EDGE,"E24.0.6.17");var subQ1=sQuery(id+"F6.wireOp",EDGE,"E24.0.6.6");var subQ2=makeQuery(id+"F6.imprint","INTERSECT",VERTEX,{"derivedFrom":[subQ1,subQ0]});Q67=makeQuery(id+"F6.imprint","IMPRINT",FACE,{"disambiguationData":[TD([[makeQuery(id+"F6.imprint","IMPRINT",EDGE,{"disambiguationData":[TD([[subQ2,-1.0]])],"derivedFrom":subQ1}),1.0]])]});}
            var Q68;
            {var subQ0=sQuery(id+"F6.wireOp",EDGE,"E24.0.6.18");var subQ1=sQuery(id+"F6.wireOp",EDGE,"E24.0.6.7");var subQ2=makeQuery(id+"F6.imprint","INTERSECT",VERTEX,{"derivedFrom":[subQ1,subQ0]});Q68=makeQuery(id+"F6.imprint","IMPRINT",FACE,{"disambiguationData":[TD([[makeQuery(id+"F6.imprint","IMPRINT",EDGE,{"disambiguationData":[TD([[subQ2,1.0]])],"derivedFrom":subQ1}),1.0]])]});}
            var Q69;
            {var subQ0=sQuery(id+"F6.wireOp",EDGE,"E24.0.6.18");var subQ1=sQuery(id+"F6.wireOp",EDGE,"E24.0.6.7");var subQ2=makeQuery(id+"F6.imprint","INTERSECT",VERTEX,{"derivedFrom":[subQ1,subQ0]});Q69=makeQuery(id+"F6.imprint","IMPRINT",FACE,{"disambiguationData":[TD([[makeQuery(id+"F6.imprint","IMPRINT",EDGE,{"disambiguationData":[TD([[subQ2,1.0]])],"derivedFrom":subQ1}),-1.0]])]});}
            var Q70;
            {var subQ0=sQuery(id+"F6.wireOp",EDGE,"E26");var subQ1=sQuery(id+"F6.wireOp",EDGE,"E24.0.6.11");var subQ2=makeQuery(id+"F6.imprint","INTERSECT",VERTEX,{"derivedFrom":[subQ1,subQ0]});Q70=makeQuery(id+"F6.imprint","IMPRINT",FACE,{"disambiguationData":[TD([[makeQuery(id+"F6.imprint","IMPRINT",EDGE,{"disambiguationData":[TD([[subQ2,1.0]])],"derivedFrom":subQ1}),1.0]])]});}
            var Q71;
            {var subQ0=sQuery(id+"F6.wireOp",EDGE,"E26");var subQ1=sQuery(id+"F6.wireOp",EDGE,"E24.0.6.11");var subQ2=makeQuery(id+"F6.imprint","INTERSECT",VERTEX,{"derivedFrom":[subQ1,subQ0]});Q71=makeQuery(id+"F6.imprint","IMPRINT",FACE,{"disambiguationData":[TD([[makeQuery(id+"F6.imprint","IMPRINT",EDGE,{"disambiguationData":[TD([[subQ2,1.0]])],"derivedFrom":subQ1}),-1.0]])]});}
            var Q72;
            {var subQ1=sQuery(id+"F6.wireOp",EDGE,"E7");var subQ3=sQuery(id+"F6.wireOp",EDGE,"E13");var subQ4=makeQuery(id+"F6.imprint","INTERSECT",VERTEX,{"derivedFrom":[subQ1,subQ3]});Q72=makeQuery(id+"F6.imprint","IMPRINT",FACE,{"disambiguationData":[TD([[makeQuery(id+"F6.imprint","IMPRINT",EDGE,{"disambiguationData":[TD([[subQ4,1.0]])],"derivedFrom":subQ3}),1.0]])]});}
            var Q73;
            {var subQ1=sQuery(id+"F6.wireOp",EDGE,"E7");var subQ3=sQuery(id+"F6.wireOp",EDGE,"E13");var subQ4=makeQuery(id+"F6.imprint","INTERSECT",VERTEX,{"derivedFrom":[subQ1,subQ3]});Q73=makeQuery(id+"F6.imprint","IMPRINT",FACE,{"disambiguationData":[TD([[makeQuery(id+"F6.imprint","IMPRINT",EDGE,{"disambiguationData":[TD([[subQ4,-1.0]])],"derivedFrom":subQ3}),1.0]])]});}
            var Q74;
            {var subQ1=sQuery(id+"F6.wireOp",EDGE,"E9");var subQ3=sQuery(id+"F6.wireOp",EDGE,"E13");var subQ4=makeQuery(id+"F6.imprint","INTERSECT",VERTEX,{"derivedFrom":[subQ1,subQ3]});Q74=makeQuery(id+"F6.imprint","IMPRINT",FACE,{"disambiguationData":[TD([[makeQuery(id+"F6.imprint","IMPRINT",EDGE,{"disambiguationData":[TD([[subQ4,1.0]])],"derivedFrom":subQ3}),1.0]])]});}
            var Q75;
            {var subQ1=sQuery(id+"F6.wireOp",EDGE,"E24.0.1.4");var subQ3=sQuery(id+"F6.wireOp",EDGE,"E24.0.1.10");var subQ4=makeQuery(id+"F6.imprint","INTERSECT",VERTEX,{"derivedFrom":[subQ1,subQ3]});Q75=makeQuery(id+"F6.imprint","IMPRINT",FACE,{"disambiguationData":[TD([[makeQuery(id+"F6.imprint","IMPRINT",EDGE,{"disambiguationData":[TD([[subQ4,-1.0]])],"derivedFrom":subQ3}),1.0]])]});}
            var Q76;
            {var subQ1=sQuery(id+"F6.wireOp",EDGE,"E24.0.1.4");var subQ3=sQuery(id+"F6.wireOp",EDGE,"E24.0.1.10");var subQ4=makeQuery(id+"F6.imprint","INTERSECT",VERTEX,{"derivedFrom":[subQ1,subQ3]});Q76=makeQuery(id+"F6.imprint","IMPRINT",FACE,{"disambiguationData":[TD([[makeQuery(id+"F6.imprint","IMPRINT",EDGE,{"disambiguationData":[TD([[subQ4,1.0]])],"derivedFrom":subQ3}),1.0]])]});}
            var Q77;
            {var subQ1=sQuery(id+"F6.wireOp",EDGE,"E24.0.1.7");var subQ3=sQuery(id+"F6.wireOp",EDGE,"E24.0.1.10");var subQ4=makeQuery(id+"F6.imprint","INTERSECT",VERTEX,{"derivedFrom":[subQ1,subQ3]});Q77=makeQuery(id+"F6.imprint","IMPRINT",FACE,{"disambiguationData":[TD([[makeQuery(id+"F6.imprint","IMPRINT",EDGE,{"disambiguationData":[TD([[subQ4,-1.0]])],"derivedFrom":subQ3}),1.0]])]});}
            var Q78;
            {var subQ1=sQuery(id+"F6.wireOp",EDGE,"E24.0.2.4");var subQ3=sQuery(id+"F6.wireOp",EDGE,"E24.0.2.10");var subQ4=makeQuery(id+"F6.imprint","INTERSECT",VERTEX,{"derivedFrom":[subQ1,subQ3]});Q78=makeQuery(id+"F6.imprint","IMPRINT",FACE,{"disambiguationData":[TD([[makeQuery(id+"F6.imprint","IMPRINT",EDGE,{"disambiguationData":[TD([[subQ4,-1.0]])],"derivedFrom":subQ3}),1.0]])]});}
            var Q79;
            {var subQ1=sQuery(id+"F6.wireOp",EDGE,"E24.0.2.4");var subQ3=sQuery(id+"F6.wireOp",EDGE,"E24.0.2.10");var subQ4=makeQuery(id+"F6.imprint","INTERSECT",VERTEX,{"derivedFrom":[subQ1,subQ3]});Q79=makeQuery(id+"F6.imprint","IMPRINT",FACE,{"disambiguationData":[TD([[makeQuery(id+"F6.imprint","IMPRINT",EDGE,{"disambiguationData":[TD([[subQ4,1.0]])],"derivedFrom":subQ3}),1.0]])]});}
            var Q80;
            {var subQ1=sQuery(id+"F6.wireOp",EDGE,"E24.0.2.7");var subQ3=sQuery(id+"F6.wireOp",EDGE,"E24.0.2.10");var subQ4=makeQuery(id+"F6.imprint","INTERSECT",VERTEX,{"derivedFrom":[subQ1,subQ3]});Q80=makeQuery(id+"F6.imprint","IMPRINT",FACE,{"disambiguationData":[TD([[makeQuery(id+"F6.imprint","IMPRINT",EDGE,{"disambiguationData":[TD([[subQ4,-1.0]])],"derivedFrom":subQ3}),1.0]])]});}
            var Q81;
            {var subQ1=sQuery(id+"F6.wireOp",EDGE,"E24.0.3.4");var subQ3=sQuery(id+"F6.wireOp",EDGE,"E24.0.3.10");var subQ4=makeQuery(id+"F6.imprint","INTERSECT",VERTEX,{"derivedFrom":[subQ1,subQ3]});Q81=makeQuery(id+"F6.imprint","IMPRINT",FACE,{"disambiguationData":[TD([[makeQuery(id+"F6.imprint","IMPRINT",EDGE,{"disambiguationData":[TD([[subQ4,-1.0]])],"derivedFrom":subQ3}),1.0]])]});}
            var Q82;
            {var subQ1=sQuery(id+"F6.wireOp",EDGE,"E24.0.3.4");var subQ3=sQuery(id+"F6.wireOp",EDGE,"E24.0.3.10");var subQ4=makeQuery(id+"F6.imprint","INTERSECT",VERTEX,{"derivedFrom":[subQ1,subQ3]});Q82=makeQuery(id+"F6.imprint","IMPRINT",FACE,{"disambiguationData":[TD([[makeQuery(id+"F6.imprint","IMPRINT",EDGE,{"disambiguationData":[TD([[subQ4,1.0]])],"derivedFrom":subQ3}),1.0]])]});}
            var Q83;
            {var subQ1=sQuery(id+"F6.wireOp",EDGE,"E24.0.3.7");var subQ3=sQuery(id+"F6.wireOp",EDGE,"E24.0.3.10");var subQ4=makeQuery(id+"F6.imprint","INTERSECT",VERTEX,{"derivedFrom":[subQ1,subQ3]});Q83=makeQuery(id+"F6.imprint","IMPRINT",FACE,{"disambiguationData":[TD([[makeQuery(id+"F6.imprint","IMPRINT",EDGE,{"disambiguationData":[TD([[subQ4,-1.0]])],"derivedFrom":subQ3}),1.0]])]});}
            var Q84;
            {var subQ1=sQuery(id+"F6.wireOp",EDGE,"E24.0.4.4");var subQ3=sQuery(id+"F6.wireOp",EDGE,"E24.0.4.10");var subQ4=makeQuery(id+"F6.imprint","INTERSECT",VERTEX,{"derivedFrom":[subQ1,subQ3]});Q84=makeQuery(id+"F6.imprint","IMPRINT",FACE,{"disambiguationData":[TD([[makeQuery(id+"F6.imprint","IMPRINT",EDGE,{"disambiguationData":[TD([[subQ4,-1.0]])],"derivedFrom":subQ3}),1.0]])]});}
            var Q85;
            {var subQ1=sQuery(id+"F6.wireOp",EDGE,"E24.0.4.4");var subQ3=sQuery(id+"F6.wireOp",EDGE,"E24.0.4.10");var subQ4=makeQuery(id+"F6.imprint","INTERSECT",VERTEX,{"derivedFrom":[subQ1,subQ3]});Q85=makeQuery(id+"F6.imprint","IMPRINT",FACE,{"disambiguationData":[TD([[makeQuery(id+"F6.imprint","IMPRINT",EDGE,{"disambiguationData":[TD([[subQ4,1.0]])],"derivedFrom":subQ3}),1.0]])]});}
            var Q86;
            {var subQ1=sQuery(id+"F6.wireOp",EDGE,"E24.0.4.7");var subQ3=sQuery(id+"F6.wireOp",EDGE,"E24.0.4.10");var subQ4=makeQuery(id+"F6.imprint","INTERSECT",VERTEX,{"derivedFrom":[subQ1,subQ3]});Q86=makeQuery(id+"F6.imprint","IMPRINT",FACE,{"disambiguationData":[TD([[makeQuery(id+"F6.imprint","IMPRINT",EDGE,{"disambiguationData":[TD([[subQ4,-1.0]])],"derivedFrom":subQ3}),1.0]])]});}
            var Q87;
            {var subQ1=sQuery(id+"F6.wireOp",EDGE,"E24.0.5.4");var subQ3=sQuery(id+"F6.wireOp",EDGE,"E24.0.5.10");var subQ4=makeQuery(id+"F6.imprint","INTERSECT",VERTEX,{"derivedFrom":[subQ1,subQ3]});Q87=makeQuery(id+"F6.imprint","IMPRINT",FACE,{"disambiguationData":[TD([[makeQuery(id+"F6.imprint","IMPRINT",EDGE,{"disambiguationData":[TD([[subQ4,-1.0]])],"derivedFrom":subQ3}),1.0]])]});}
            var Q88;
            {var subQ1=sQuery(id+"F6.wireOp",EDGE,"E24.0.5.4");var subQ3=sQuery(id+"F6.wireOp",EDGE,"E24.0.5.10");var subQ4=makeQuery(id+"F6.imprint","INTERSECT",VERTEX,{"derivedFrom":[subQ1,subQ3]});Q88=makeQuery(id+"F6.imprint","IMPRINT",FACE,{"disambiguationData":[TD([[makeQuery(id+"F6.imprint","IMPRINT",EDGE,{"disambiguationData":[TD([[subQ4,1.0]])],"derivedFrom":subQ3}),1.0]])]});}
            var Q89;
            {var subQ1=sQuery(id+"F6.wireOp",EDGE,"E24.0.5.7");var subQ3=sQuery(id+"F6.wireOp",EDGE,"E24.0.5.10");var subQ4=makeQuery(id+"F6.imprint","INTERSECT",VERTEX,{"derivedFrom":[subQ1,subQ3]});Q89=makeQuery(id+"F6.imprint","IMPRINT",FACE,{"disambiguationData":[TD([[makeQuery(id+"F6.imprint","IMPRINT",EDGE,{"disambiguationData":[TD([[subQ4,-1.0]])],"derivedFrom":subQ3}),1.0]])]});}
            var Q90;
            {var subQ1=sQuery(id+"F6.wireOp",EDGE,"E24.0.6.7");var subQ3=sQuery(id+"F6.wireOp",EDGE,"E24.0.6.10");var subQ4=makeQuery(id+"F6.imprint","INTERSECT",VERTEX,{"derivedFrom":[subQ1,subQ3]});Q90=makeQuery(id+"F6.imprint","IMPRINT",FACE,{"disambiguationData":[TD([[makeQuery(id+"F6.imprint","IMPRINT",EDGE,{"disambiguationData":[TD([[subQ4,-1.0]])],"derivedFrom":subQ3}),1.0]])]});}
            var Q91;
            {var subQ1=sQuery(id+"F6.wireOp",EDGE,"E24.0.6.4");var subQ3=sQuery(id+"F6.wireOp",EDGE,"E24.0.6.10");var subQ4=makeQuery(id+"F6.imprint","INTERSECT",VERTEX,{"derivedFrom":[subQ1,subQ3]});Q91=makeQuery(id+"F6.imprint","IMPRINT",FACE,{"disambiguationData":[TD([[makeQuery(id+"F6.imprint","IMPRINT",EDGE,{"disambiguationData":[TD([[subQ4,1.0]])],"derivedFrom":subQ3}),1.0]])]});}
            var Q92;
            {var subQ1=sQuery(id+"F6.wireOp",EDGE,"E24.0.6.4");var subQ3=sQuery(id+"F6.wireOp",EDGE,"E24.0.6.10");var subQ4=makeQuery(id+"F6.imprint","INTERSECT",VERTEX,{"derivedFrom":[subQ1,subQ3]});Q92=makeQuery(id+"F6.imprint","IMPRINT",FACE,{"disambiguationData":[TD([[makeQuery(id+"F6.imprint","IMPRINT",EDGE,{"disambiguationData":[TD([[subQ4,-1.0]])],"derivedFrom":subQ3}),1.0]])]});}
            extrude(context, id + "F7", {"entities" : qUnion([Q0, Q1, Q2, Q3, Q4, Q5, Q6, Q7, Q8, Q9, Q10, Q11, Q12, Q13, Q14, Q15, Q16, Q17, Q18, Q19, Q20, Q21, Q22, Q23, Q24, Q25, Q26, Q27, Q28, Q29, Q30, Q31, Q32, Q33, Q34, Q35, Q36, Q37, Q38, Q39, Q40, Q41, Q42, Q43, Q44, Q45, Q46, Q47, Q48, Q49, Q50, Q51, Q52, Q53, Q54, Q55, Q56, Q57, Q58, Q59, Q60, Q61, Q62, Q63, Q64, Q65, Q66, Q67, Q68, Q69, Q70, Q71, Q72, Q73, Q74, Q75, Q76, Q77, Q78, Q79, Q80, Q81, Q82, Q83, Q84, Q85, Q86, Q87, Q88, Q89, Q90, Q91, Q92]), "operationType" : NewBodyOperationType.REMOVE, "oppositeDirection" : true, "depth" : 3 * mm});
        }
        {
            var Q0;
            Q0=makeQuery(id+"F3.boolean.opBoolean","MERGE",FACE,{"derivedFrom":[makeQuery(id+"F1.opExtrude","SWEPT_FACE",FACE,{"disambiguationData":[OSD([sQuery(id+"F0.wireOp",EDGE,"E0.right")])]}),makeQuery(id+"F3.opExtrude","SWEPT_FACE",FACE,{"disambiguationData":[OSD([sQuery(id+"F2.wireOp",EDGE,"E2.right")])]})]});
            var sketch = newSketch(context, id + "F8", { "sketchPlane" : qUnion([Q0])});
            skLineSegment(sketch, "E28", {"start": v(-25.5, 117) * mm, "end": v(-25.5, 109) * mm});
            skLineSegment(sketch, "E29", {"start": v(-25.5, 109) * mm, "end": v(25.5, 109) * mm});
            skPoint(sketch, "E30.middle", {"position": v(0, 109) * mm});
            skLineSegment(sketch, "E31", {"start": v(0, 109) * mm, "end": v(-25.5, 109) * mm});
            skLineSegment(sketch, "E32", {"start": v(0, 109) * mm, "end": v(25.5, 109) * mm});
            skCircle(sketch, "E33", {"center": v(-12.75, 109) * mm, "radius": 3 * mm});
            skCircle(sketch, "E34", {"center": v(0, 109) * mm, "radius": 3 * mm});
            skCircle(sketch, "E35", {"center": v(12.75, 109) * mm, "radius": 3 * mm});
            skSolve(sketch);
        }
        {
            var Q0;
            Q0 = qSketchRegion(id + "F8", true);
            extrude(context, id + "F9", {"entities" : qUnion([Q0]), "operationType" : NewBodyOperationType.REMOVE, "oppositeDirection" : true, "depth" : 106.1 * mm});
        }
        {
            var Q0;
            Q0=makeQuery(id+"F3.boolean.opBoolean","MERGE",FACE,{"derivedFrom":[makeQuery(id+"F1.opExtrude","SWEPT_FACE",FACE,{"disambiguationData":[OSD([sQuery(id+"F0.wireOp",EDGE,"E0.right")])]}),makeQuery(id+"F3.opExtrude","SWEPT_FACE",FACE,{"disambiguationData":[OSD([sQuery(id+"F2.wireOp",EDGE,"E2.right")])]})]});
            var sketch = newSketch(context, id + "F10", { "sketchPlane" : qUnion([Q0])});
            skLineSegment(sketch, "E36", {"start": v(0, 0) * mm, "end": v(0, 3) * mm});
            skLineSegment(sketch, "E37", {"start": v(-25.5, 3) * mm, "end": v(25.5, 3) * mm});
            skLineSegment(sketch, "E38", {"start": v(0, 117) * mm, "end": v(-25.5, 117) * mm});
            skLineSegment(sketch, "E39", {"start": v(0, 117) * mm, "end": v(25.5, 117) * mm});
            skLineSegment(sketch, "E40", {"start": v(-22.5, 7.47) * mm, "end": v(-18.5, 3) * mm});
            skLineSegment(sketch, "E41", {"start": v(22.5, 7.69) * mm, "end": v(18.76, 3) * mm});
            skLineSegment(sketch, "E42", {"start": v(18.76, 3) * mm, "end": v(-22.5, 44.26) * mm});
            skLineSegment(sketch, "E43", {"start": v(22.5, 7.69) * mm, "end": v(-22.5, 52.69) * mm});
            skLineSegment(sketch, "E44", {"start": v(-22.5, 7.47) * mm, "end": v(22.71, 52.69) * mm});
            skLineSegment(sketch, "E45", {"start": v(-18.5, 3) * mm, "end": v(22.6, 44.1) * mm});
            skLineSegment(sketch, "E46", {"start": v(22.71, 52.69) * mm, "end": v(-22.5, 97.9) * mm});
            skLineSegment(sketch, "E47", {"start": v(-22.5, 52.69) * mm, "end": v(22.6, 97.78) * mm});
            skLineSegment(sketch, "E48", {"start": v(22.6, 97.78) * mm, "end": v(18.35, 102.03) * mm});
            skLineSegment(sketch, "E49", {"start": v(18.35, 102.03) * mm, "end": v(-22.5, 61.18) * mm});
            skLineSegment(sketch, "E50", {"start": v(-22.5, 97.9) * mm, "end": v(-18.25, 102.13) * mm});
            skLineSegment(sketch, "E51", {"start": v(-18.25, 102.13) * mm, "end": v(22.71, 61.17) * mm});
            skLineSegment(sketch, "E52", {"start": v(25.5, 117) * mm, "end": v(19.5, 117) * mm});
            skLineSegment(sketch, "E53", {"start": v(22.5, 3) * mm, "end": v(22.5, 117) * mm});
            skLineSegment(sketch, "E54", {"start": v(-22.5, 117) * mm, "end": v(-22.5, 3) * mm});
            skLineSegment(sketch, "E55", {"start": v(22.5, 102.03) * mm, "end": v(-22.5, 102.03) * mm});
            skLineSegment(sketch, "E56", {"start": v(0, 117) * mm, "end": v(0, 83.67) * mm});
            skLineSegment(sketch, "E57", {"start": v(0, 102.03) * mm, "end": v(-9.07, 92.95) * mm});
            skLineSegment(sketch, "E58", {"start": v(0, 102.03) * mm, "end": v(9.18, 92.85) * mm});
            skSolve(sketch);
        }
        {
            var Q0;
            {var subQ0=sQuery(id+"F10.wireOp",EDGE,"E54");var subQ3=sQuery(id+"F10.wireOp",EDGE,"E49");var subQ5=makeQuery(id+"F10.imprint","INTERSECT",VERTEX,{"derivedFrom":[subQ3,subQ0]});Q0=makeQuery(id+"F10.imprint","IMPRINT",FACE,{"disambiguationData":[TD([[makeQuery(id+"F10.imprint","IMPRINT",EDGE,{"disambiguationData":[TD([[subQ5,1.0]])],"derivedFrom":subQ3}),-1.0]])]});}
            var Q1;
            {var subQ0=sQuery(id+"F10.wireOp",EDGE,"E51");var subQ1=sQuery(id+"F10.wireOp",EDGE,"E47");var subQ2=makeQuery(id+"F10.imprint","INTERSECT",VERTEX,{"derivedFrom":[subQ1,subQ0]});Q1=makeQuery(id+"F10.imprint","IMPRINT",FACE,{"disambiguationData":[TD([[makeQuery(id+"F10.imprint","IMPRINT",EDGE,{"disambiguationData":[TD([[subQ2,-1.0]])],"derivedFrom":subQ1}),-1.0]])]});}
            var Q2;
            {var subQ7=sQuery(id+"F10.wireOp",EDGE,"E44");var subQ8=sQuery(id+"F10.wireOp",EDGE,"E43");var subQ9=makeQuery(id+"F10.imprint","INTERSECT",VERTEX,{"derivedFrom":[subQ8,subQ7]});Q2=makeQuery(id+"F10.imprint","IMPRINT",FACE,{"disambiguationData":[TD([[makeQuery(id+"F10.imprint","IMPRINT",EDGE,{"disambiguationData":[TD([[subQ9,-1.0]])],"derivedFrom":subQ8}),-1.0]])]});}
            var Q3;
            {var subQ0=sQuery(id+"F10.wireOp",EDGE,"E54");var subQ1=sQuery(id+"F10.wireOp",EDGE,"E42");var subQ2=makeQuery(id+"F10.imprint","INTERSECT",VERTEX,{"derivedFrom":[subQ1,subQ0]});Q3=makeQuery(id+"F10.imprint","IMPRINT",FACE,{"disambiguationData":[TD([[makeQuery(id+"F10.imprint","IMPRINT",EDGE,{"disambiguationData":[TD([[subQ2,1.0]])],"derivedFrom":subQ1}),1.0]])]});}
            var Q4;
            {var subQ0=sQuery(id+"F10.wireOp",EDGE,"E37");var subQ1=makeQuery(id+"F10.imprint","INTERSECT",VERTEX,{"derivedFrom":[sQuery(id+"F10.wireOp",EDGE,"E36"),subQ0]});Q4=makeQuery(id+"F10.imprint","IMPRINT",FACE,{"disambiguationData":[TD([[makeQuery(id+"F10.imprint","IMPRINT",EDGE,{"disambiguationData":[TD([[subQ1,1.0]])],"derivedFrom":subQ0}),1.0]])]});}
            var Q5;
            {var subQ0=sQuery(id+"F10.wireOp",EDGE,"E53");var subQ3=sQuery(id+"F10.wireOp",EDGE,"E45");var subQ5=makeQuery(id+"F10.imprint","INTERSECT",VERTEX,{"derivedFrom":[subQ3,subQ0]});Q5=makeQuery(id+"F10.imprint","IMPRINT",FACE,{"disambiguationData":[TD([[makeQuery(id+"F10.imprint","IMPRINT",EDGE,{"disambiguationData":[TD([[subQ5,1.0]])],"derivedFrom":subQ3}),-1.0]])]});}
            var Q6;
            {var subQ0=sQuery(id+"F10.wireOp",EDGE,"E57");var subQ1=sQuery(id+"F10.wireOp",EDGE,"E51");var subQ2=makeQuery(id+"F10.imprint","INTERSECT",VERTEX,{"derivedFrom":[subQ1,subQ0]});Q6=makeQuery(id+"F10.imprint","IMPRINT",FACE,{"disambiguationData":[TD([[makeQuery(id+"F10.imprint","IMPRINT",EDGE,{"disambiguationData":[TD([[subQ2,-1.0]])],"derivedFrom":subQ1}),1.0]])]});}
            var Q7;
            {var subQ0=sQuery(id+"F10.wireOp",EDGE,"E58");Q7=makeQuery(id+"F10.imprint","IMPRINT",FACE,{"disambiguationData":[TD([[makeQuery(id+"F10.imprint","IMPRINT",EDGE,{"derivedFrom":subQ0}),-1.0]])]});}
            extrude(context, id + "F11", {"entities" : qUnion([Q0, Q1, Q2, Q3, Q4, Q5, Q6, Q7]), "operationType" : NewBodyOperationType.REMOVE, "endBound" : BoundingType.THROUGH_ALL, "oppositeDirection" : true, "depth" : 25 * mm});
        }
        {
            var Q0;
            Q0=makeQuery(id+"F1.opExtrude","CAP_FACE",FACE,{"disambiguationData":[OSD([sQuery(id+"F0.wireOp",EDGE,"E0.bottom"),sQuery(id+"F0.wireOp",EDGE,"E0.top"),sQuery(id+"F0.wireOp",EDGE,"E0.left"),sQuery(id+"F0.wireOp",EDGE,"E0.right")])],"isStart":true});
            var sketch = newSketch(context, id + "F12", { "sketchPlane" : qUnion([Q0])});
            skLineSegment(sketch, "E59", {"start": v(0, -25.5) * mm, "end": v(0, -16) * mm});
            skPoint(sketch, "E59.endSnap0", {"position": v(0, -25.5) * mm});
            skLineSegment(sketch, "E60", {"start": v(0, -16) * mm, "end": v(8, -16) * mm});
            skLineSegment(sketch, "E61", {"start": v(8, -16) * mm, "end": v(16, -16) * mm});
            skLineSegment(sketch, "E62", {"start": v(0, -16) * mm, "end": v(-8, -16) * mm});
            skLineSegment(sketch, "E63", {"start": v(-8, -16) * mm, "end": v(-16, -16) * mm});
            skCircle(sketch, "E64", {"center": v(16, -16) * mm, "radius": 2.1 * mm});
            skCircle(sketch, "E65", {"center": v(8, -16) * mm, "radius": 2.1 * mm});
            skCircle(sketch, "E66", {"center": v(0, -16) * mm, "radius": 2.1 * mm});
            skCircle(sketch, "E67", {"center": v(-8, -16) * mm, "radius": 2.1 * mm});
            skCircle(sketch, "E68", {"center": v(-16, -16) * mm, "radius": 2.1 * mm});
            skLineSegment(sketch, "E69", {"start": v(12, -16) * mm, "end": v(12, -8) * mm});
            skLineSegment(sketch, "E70", {"start": v(12, -8) * mm, "end": v(4, -8) * mm});
            skLineSegment(sketch, "E71", {"start": v(4, -8) * mm, "end": v(-4, -8) * mm});
            skLineSegment(sketch, "E72", {"start": v(-4, -8) * mm, "end": v(-12, -8) * mm});
            skCircle(sketch, "E73", {"center": v(12, -8) * mm, "radius": 2.1 * mm});
            skCircle(sketch, "E74", {"center": v(4, -8) * mm, "radius": 2.1 * mm});
            skCircle(sketch, "E75", {"center": v(-4, -8) * mm, "radius": 2.1 * mm});
            skCircle(sketch, "E76", {"center": v(-12, -8) * mm, "radius": 2.1 * mm});
            skCircle(sketch, "E77.0.1.0", {"center": v(-12, 8) * mm, "radius": 2.1 * mm});
            skLineSegment(sketch, "E77.0.1.1", {"start": v(-8, 0) * mm, "end": v(-16, 0) * mm});
            skLineSegment(sketch, "E77.0.1.2", {"start": v(-4, 8) * mm, "end": v(-12, 8) * mm});
            skCircle(sketch, "E77.0.1.3", {"center": v(16, 0) * mm, "radius": 2.1 * mm});
            skCircle(sketch, "E77.0.1.4", {"center": v(8, 0) * mm, "radius": 2.1 * mm});
            skCircle(sketch, "E77.0.1.5", {"center": v(0, 0) * mm, "radius": 2.1 * mm});
            skCircle(sketch, "E77.0.1.6", {"center": v(-8, 0) * mm, "radius": 2.1 * mm});
            skCircle(sketch, "E77.0.1.7", {"center": v(-16, 0) * mm, "radius": 2.1 * mm});
            skLineSegment(sketch, "E77.0.1.8", {"start": v(12, 0) * mm, "end": v(12, 8) * mm});
            skLineSegment(sketch, "E77.0.1.9", {"start": v(12, 8) * mm, "end": v(4, 8) * mm});
            skLineSegment(sketch, "E77.0.1.10", {"start": v(4, 8) * mm, "end": v(-4, 8) * mm});
            skCircle(sketch, "E77.0.1.11", {"center": v(12, 8) * mm, "radius": 2.1 * mm});
            skCircle(sketch, "E77.0.1.12", {"center": v(-4, 8) * mm, "radius": 2.1 * mm});
            skLineSegment(sketch, "E77.0.1.13", {"start": v(0, 0) * mm, "end": v(-8, 0) * mm});
            skLineSegment(sketch, "E77.0.1.14", {"start": v(8, 0) * mm, "end": v(16, 0) * mm});
            skLineSegment(sketch, "E77.0.1.15", {"start": v(0, 0) * mm, "end": v(8, 0) * mm});
            skCircle(sketch, "E77.0.1.16", {"center": v(4, 8) * mm, "radius": 2.1 * mm});
            skLineSegment(sketch, "E77.0.2.1", {"start": v(-8, 16) * mm, "end": v(-16, 16) * mm});
            skCircle(sketch, "E77.0.2.3", {"center": v(16, 16) * mm, "radius": 2.1 * mm});
            skCircle(sketch, "E77.0.2.4", {"center": v(8, 16) * mm, "radius": 2.1 * mm});
            skCircle(sketch, "E77.0.2.5", {"center": v(0, 16) * mm, "radius": 2.1 * mm});
            skCircle(sketch, "E77.0.2.6", {"center": v(-8, 16) * mm, "radius": 2.1 * mm});
            skCircle(sketch, "E77.0.2.7", {"center": v(-16, 16) * mm, "radius": 2.1 * mm});
            skLineSegment(sketch, "E77.0.2.13", {"start": v(0, 16) * mm, "end": v(-8, 16) * mm});
            skLineSegment(sketch, "E77.0.2.14", {"start": v(8, 16) * mm, "end": v(16, 16) * mm});
            skLineSegment(sketch, "E77.0.2.15", {"start": v(0, 16) * mm, "end": v(8, 16) * mm});
            skLineSegment(sketch, "E77.direction1", {"start": v(-16, -16) * mm, "end": v(9, -16) * mm, "construction": true});
            skLineSegment(sketch, "E77.direction2", {"start": v(-16, -16) * mm, "end": v(-16, 0) * mm, "construction": true});
            skLineSegment(sketch, "E78", {"start": v(-16, 16) * mm, "end": v(-16, 25.5) * mm});
            skSolve(sketch);
        }
        {
            var Q0;
            Q0=makeQuery(id+"F12.imprint","IMPRINT",FACE,{"disambiguationData":[TD([[makeQuery(id+"F12.imprint","IMPRINT",EDGE,{"derivedFrom":sQuery(id+"F12.wireOp",EDGE,"E64")}),1.0]])]});
            var Q1;
            {var subQ0=sQuery(id+"F12.wireOp",EDGE,"E61");var subQ1=sQuery(id+"F12.wireOp",EDGE,"E60");var subQ2=makeQuery(id+"F12.imprint","INTERSECT",VERTEX,{"derivedFrom":[subQ1,subQ0]});Q1=makeQuery(id+"F12.imprint","IMPRINT",FACE,{"disambiguationData":[TD([[makeQuery(id+"F12.imprint","IMPRINT",EDGE,{"disambiguationData":[TD([[subQ2,1.0]])],"derivedFrom":subQ1}),1.0]])]});}
            var Q2;
            {var subQ0=sQuery(id+"F12.wireOp",EDGE,"E61");var subQ1=sQuery(id+"F12.wireOp",EDGE,"E60");var subQ2=makeQuery(id+"F12.imprint","INTERSECT",VERTEX,{"derivedFrom":[subQ1,subQ0]});Q2=makeQuery(id+"F12.imprint","IMPRINT",FACE,{"disambiguationData":[TD([[makeQuery(id+"F12.imprint","IMPRINT",EDGE,{"disambiguationData":[TD([[subQ2,1.0]])],"derivedFrom":subQ1}),-1.0]])]});}
            var Q3;
            {var subQ1=sQuery(id+"F12.wireOp",EDGE,"E60");var subQ3=sQuery(id+"F12.wireOp",EDGE,"E66");var subQ4=makeQuery(id+"F12.imprint","INTERSECT",VERTEX,{"derivedFrom":[subQ1,subQ3]});Q3=makeQuery(id+"F12.imprint","IMPRINT",FACE,{"disambiguationData":[TD([[makeQuery(id+"F12.imprint","IMPRINT",EDGE,{"disambiguationData":[TD([[subQ4,-1.0]])],"derivedFrom":subQ3}),1.0]])]});}
            var Q4;
            {var subQ1=sQuery(id+"F12.wireOp",EDGE,"E59");var subQ3=sQuery(id+"F12.wireOp",EDGE,"E66");var subQ4=makeQuery(id+"F12.imprint","INTERSECT",VERTEX,{"derivedFrom":[subQ1,subQ3]});Q4=makeQuery(id+"F12.imprint","IMPRINT",FACE,{"disambiguationData":[TD([[makeQuery(id+"F12.imprint","IMPRINT",EDGE,{"disambiguationData":[TD([[subQ4,-1.0]])],"derivedFrom":subQ3}),1.0]])]});}
            var Q5;
            {var subQ1=sQuery(id+"F12.wireOp",EDGE,"E59");var subQ3=sQuery(id+"F12.wireOp",EDGE,"E66");var subQ4=makeQuery(id+"F12.imprint","INTERSECT",VERTEX,{"derivedFrom":[subQ1,subQ3]});Q5=makeQuery(id+"F12.imprint","IMPRINT",FACE,{"disambiguationData":[TD([[makeQuery(id+"F12.imprint","IMPRINT",EDGE,{"disambiguationData":[TD([[subQ4,1.0]])],"derivedFrom":subQ3}),1.0]])]});}
            var Q6;
            {var subQ0=sQuery(id+"F12.wireOp",EDGE,"E63");var subQ1=sQuery(id+"F12.wireOp",EDGE,"E62");var subQ2=makeQuery(id+"F12.imprint","INTERSECT",VERTEX,{"derivedFrom":[subQ1,subQ0]});Q6=makeQuery(id+"F12.imprint","IMPRINT",FACE,{"disambiguationData":[TD([[makeQuery(id+"F12.imprint","IMPRINT",EDGE,{"disambiguationData":[TD([[subQ2,1.0]])],"derivedFrom":subQ1}),1.0]])]});}
            var Q7;
            {var subQ0=sQuery(id+"F12.wireOp",EDGE,"E63");var subQ1=sQuery(id+"F12.wireOp",EDGE,"E62");var subQ2=makeQuery(id+"F12.imprint","INTERSECT",VERTEX,{"derivedFrom":[subQ1,subQ0]});Q7=makeQuery(id+"F12.imprint","IMPRINT",FACE,{"disambiguationData":[TD([[makeQuery(id+"F12.imprint","IMPRINT",EDGE,{"disambiguationData":[TD([[subQ2,1.0]])],"derivedFrom":subQ1}),-1.0]])]});}
            var Q8;
            Q8=makeQuery(id+"F12.imprint","IMPRINT",FACE,{"disambiguationData":[TD([[makeQuery(id+"F12.imprint","IMPRINT",EDGE,{"derivedFrom":sQuery(id+"F12.wireOp",EDGE,"E68")}),1.0]])]});
            var Q9;
            Q9=makeQuery(id+"F12.imprint","IMPRINT",FACE,{"disambiguationData":[TD([[makeQuery(id+"F12.imprint","IMPRINT",EDGE,{"derivedFrom":sQuery(id+"F12.wireOp",EDGE,"E76")}),1.0]])]});
            var Q10;
            {var subQ0=sQuery(id+"F12.wireOp",EDGE,"E72");var subQ1=sQuery(id+"F12.wireOp",EDGE,"E71");var subQ2=makeQuery(id+"F12.imprint","INTERSECT",VERTEX,{"derivedFrom":[subQ1,subQ0]});Q10=makeQuery(id+"F12.imprint","IMPRINT",FACE,{"disambiguationData":[TD([[makeQuery(id+"F12.imprint","IMPRINT",EDGE,{"disambiguationData":[TD([[subQ2,1.0]])],"derivedFrom":subQ1}),1.0]])]});}
            var Q11;
            {var subQ0=sQuery(id+"F12.wireOp",EDGE,"E72");var subQ1=sQuery(id+"F12.wireOp",EDGE,"E71");var subQ2=makeQuery(id+"F12.imprint","INTERSECT",VERTEX,{"derivedFrom":[subQ1,subQ0]});Q11=makeQuery(id+"F12.imprint","IMPRINT",FACE,{"disambiguationData":[TD([[makeQuery(id+"F12.imprint","IMPRINT",EDGE,{"disambiguationData":[TD([[subQ2,1.0]])],"derivedFrom":subQ1}),-1.0]])]});}
            var Q12;
            {var subQ0=sQuery(id+"F12.wireOp",EDGE,"E71");var subQ1=sQuery(id+"F12.wireOp",EDGE,"E70");var subQ2=makeQuery(id+"F12.imprint","INTERSECT",VERTEX,{"derivedFrom":[subQ1,subQ0]});Q12=makeQuery(id+"F12.imprint","IMPRINT",FACE,{"disambiguationData":[TD([[makeQuery(id+"F12.imprint","IMPRINT",EDGE,{"disambiguationData":[TD([[subQ2,1.0]])],"derivedFrom":subQ1}),-1.0]])]});}
            var Q13;
            {var subQ0=sQuery(id+"F12.wireOp",EDGE,"E71");var subQ1=sQuery(id+"F12.wireOp",EDGE,"E70");var subQ2=makeQuery(id+"F12.imprint","INTERSECT",VERTEX,{"derivedFrom":[subQ1,subQ0]});Q13=makeQuery(id+"F12.imprint","IMPRINT",FACE,{"disambiguationData":[TD([[makeQuery(id+"F12.imprint","IMPRINT",EDGE,{"disambiguationData":[TD([[subQ2,1.0]])],"derivedFrom":subQ1}),1.0]])]});}
            var Q14;
            {var subQ0=sQuery(id+"F12.wireOp",EDGE,"E70");var subQ1=sQuery(id+"F12.wireOp",EDGE,"E69");var subQ2=makeQuery(id+"F12.imprint","INTERSECT",VERTEX,{"derivedFrom":[subQ1,subQ0]});Q14=makeQuery(id+"F12.imprint","IMPRINT",FACE,{"disambiguationData":[TD([[makeQuery(id+"F12.imprint","IMPRINT",EDGE,{"disambiguationData":[TD([[subQ2,1.0]])],"derivedFrom":subQ1}),-1.0]])]});}
            var Q15;
            {var subQ0=sQuery(id+"F12.wireOp",EDGE,"E70");var subQ1=sQuery(id+"F12.wireOp",EDGE,"E69");var subQ2=makeQuery(id+"F12.imprint","INTERSECT",VERTEX,{"derivedFrom":[subQ1,subQ0]});Q15=makeQuery(id+"F12.imprint","IMPRINT",FACE,{"disambiguationData":[TD([[makeQuery(id+"F12.imprint","IMPRINT",EDGE,{"disambiguationData":[TD([[subQ2,1.0]])],"derivedFrom":subQ1}),1.0]])]});}
            var Q16;
            Q16=makeQuery(id+"F12.imprint","IMPRINT",FACE,{"disambiguationData":[TD([[makeQuery(id+"F12.imprint","IMPRINT",EDGE,{"derivedFrom":sQuery(id+"F12.wireOp",EDGE,"E77.0.1.3")}),1.0]])]});
            var Q17;
            {var subQ0=sQuery(id+"F12.wireOp",EDGE,"E77.0.1.14");var subQ1=sQuery(id+"F12.wireOp",EDGE,"E77.0.1.4");var subQ2=makeQuery(id+"F12.imprint","INTERSECT",VERTEX,{"derivedFrom":[subQ1,subQ0]});Q17=makeQuery(id+"F12.imprint","IMPRINT",FACE,{"disambiguationData":[TD([[makeQuery(id+"F12.imprint","IMPRINT",EDGE,{"disambiguationData":[TD([[subQ2,-1.0]])],"derivedFrom":subQ1}),1.0]])]});}
            var Q18;
            {var subQ0=sQuery(id+"F12.wireOp",EDGE,"E77.0.1.14");var subQ1=sQuery(id+"F12.wireOp",EDGE,"E77.0.1.4");var subQ2=makeQuery(id+"F12.imprint","INTERSECT",VERTEX,{"derivedFrom":[subQ1,subQ0]});Q18=makeQuery(id+"F12.imprint","IMPRINT",FACE,{"disambiguationData":[TD([[makeQuery(id+"F12.imprint","IMPRINT",EDGE,{"disambiguationData":[TD([[subQ2,1.0]])],"derivedFrom":subQ1}),1.0]])]});}
            var Q19;
            {var subQ0=sQuery(id+"F12.wireOp",EDGE,"E77.0.1.13");var subQ1=sQuery(id+"F12.wireOp",EDGE,"E77.0.1.5");var subQ2=makeQuery(id+"F12.imprint","INTERSECT",VERTEX,{"derivedFrom":[subQ1,subQ0]});Q19=makeQuery(id+"F12.imprint","IMPRINT",FACE,{"disambiguationData":[TD([[makeQuery(id+"F12.imprint","IMPRINT",EDGE,{"disambiguationData":[TD([[subQ2,-1.0]])],"derivedFrom":subQ1}),1.0]])]});}
            var Q20;
            {var subQ0=sQuery(id+"F12.wireOp",EDGE,"E77.0.1.13");var subQ1=sQuery(id+"F12.wireOp",EDGE,"E77.0.1.5");var subQ2=makeQuery(id+"F12.imprint","INTERSECT",VERTEX,{"derivedFrom":[subQ1,subQ0]});Q20=makeQuery(id+"F12.imprint","IMPRINT",FACE,{"disambiguationData":[TD([[makeQuery(id+"F12.imprint","IMPRINT",EDGE,{"disambiguationData":[TD([[subQ2,1.0]])],"derivedFrom":subQ1}),1.0]])]});}
            var Q21;
            {var subQ0=sQuery(id+"F12.wireOp",EDGE,"E77.0.1.13");var subQ1=sQuery(id+"F12.wireOp",EDGE,"E77.0.1.1");var subQ2=makeQuery(id+"F12.imprint","INTERSECT",VERTEX,{"derivedFrom":[subQ1,subQ0]});Q21=makeQuery(id+"F12.imprint","IMPRINT",FACE,{"disambiguationData":[TD([[makeQuery(id+"F12.imprint","IMPRINT",EDGE,{"disambiguationData":[TD([[subQ2,-1.0]])],"derivedFrom":subQ1}),-1.0]])]});}
            var Q22;
            Q22=makeQuery(id+"F12.imprint","IMPRINT",FACE,{"disambiguationData":[TD([[makeQuery(id+"F12.imprint","IMPRINT",EDGE,{"derivedFrom":sQuery(id+"F12.wireOp",EDGE,"E77.0.1.7")}),1.0]])]});
            var Q23;
            Q23=makeQuery(id+"F12.imprint","IMPRINT",FACE,{"disambiguationData":[TD([[makeQuery(id+"F12.imprint","IMPRINT",EDGE,{"derivedFrom":sQuery(id+"F12.wireOp",EDGE,"E77.0.1.0")}),1.0]])]});
            var Q24;
            {var subQ0=sQuery(id+"F12.wireOp",EDGE,"E77.0.1.10");var subQ1=sQuery(id+"F12.wireOp",EDGE,"E77.0.1.2");var subQ2=makeQuery(id+"F12.imprint","INTERSECT",VERTEX,{"derivedFrom":[subQ1,subQ0]});Q24=makeQuery(id+"F12.imprint","IMPRINT",FACE,{"disambiguationData":[TD([[makeQuery(id+"F12.imprint","IMPRINT",EDGE,{"disambiguationData":[TD([[subQ2,-1.0]])],"derivedFrom":subQ1}),-1.0]])]});}
            var Q25;
            {var subQ0=sQuery(id+"F12.wireOp",EDGE,"E77.0.1.10");var subQ1=sQuery(id+"F12.wireOp",EDGE,"E77.0.1.2");var subQ2=makeQuery(id+"F12.imprint","INTERSECT",VERTEX,{"derivedFrom":[subQ1,subQ0]});Q25=makeQuery(id+"F12.imprint","IMPRINT",FACE,{"disambiguationData":[TD([[makeQuery(id+"F12.imprint","IMPRINT",EDGE,{"disambiguationData":[TD([[subQ2,-1.0]])],"derivedFrom":subQ1}),1.0]])]});}
            var Q26;
            {var subQ0=sQuery(id+"F12.wireOp",EDGE,"E77.0.1.10");var subQ1=sQuery(id+"F12.wireOp",EDGE,"E77.0.1.9");var subQ2=makeQuery(id+"F12.imprint","INTERSECT",VERTEX,{"derivedFrom":[subQ1,subQ0]});Q26=makeQuery(id+"F12.imprint","IMPRINT",FACE,{"disambiguationData":[TD([[makeQuery(id+"F12.imprint","IMPRINT",EDGE,{"disambiguationData":[TD([[subQ2,1.0]])],"derivedFrom":subQ1}),1.0]])]});}
            var Q27;
            {var subQ0=sQuery(id+"F12.wireOp",EDGE,"E77.0.1.10");var subQ1=sQuery(id+"F12.wireOp",EDGE,"E77.0.1.9");var subQ2=makeQuery(id+"F12.imprint","INTERSECT",VERTEX,{"derivedFrom":[subQ1,subQ0]});Q27=makeQuery(id+"F12.imprint","IMPRINT",FACE,{"disambiguationData":[TD([[makeQuery(id+"F12.imprint","IMPRINT",EDGE,{"disambiguationData":[TD([[subQ2,1.0]])],"derivedFrom":subQ1}),-1.0]])]});}
            var Q28;
            {var subQ0=sQuery(id+"F12.wireOp",EDGE,"E77.0.1.9");var subQ1=sQuery(id+"F12.wireOp",EDGE,"E77.0.1.8");var subQ2=makeQuery(id+"F12.imprint","INTERSECT",VERTEX,{"derivedFrom":[subQ1,subQ0]});Q28=makeQuery(id+"F12.imprint","IMPRINT",FACE,{"disambiguationData":[TD([[makeQuery(id+"F12.imprint","IMPRINT",EDGE,{"disambiguationData":[TD([[subQ2,1.0]])],"derivedFrom":subQ1}),-1.0]])]});}
            var Q29;
            {var subQ0=sQuery(id+"F12.wireOp",EDGE,"E78");var subQ1=sQuery(id+"F12.wireOp",EDGE,"E77.0.2.1");var subQ2=makeQuery(id+"F12.imprint","INTERSECT",VERTEX,{"derivedFrom":[subQ1,subQ0]});Q29=makeQuery(id+"F12.imprint","IMPRINT",FACE,{"disambiguationData":[TD([[makeQuery(id+"F12.imprint","IMPRINT",EDGE,{"disambiguationData":[TD([[subQ2,1.0]])],"derivedFrom":subQ1}),1.0]])]});}
            var Q30;
            {var subQ0=sQuery(id+"F12.wireOp",EDGE,"E78");var subQ1=sQuery(id+"F12.wireOp",EDGE,"E77.0.2.1");var subQ2=makeQuery(id+"F12.imprint","INTERSECT",VERTEX,{"derivedFrom":[subQ1,subQ0]});Q30=makeQuery(id+"F12.imprint","IMPRINT",FACE,{"disambiguationData":[TD([[makeQuery(id+"F12.imprint","IMPRINT",EDGE,{"disambiguationData":[TD([[subQ2,1.0]])],"derivedFrom":subQ1}),-1.0]])]});}
            var Q31;
            {var subQ0=sQuery(id+"F12.wireOp",EDGE,"E77.0.2.13");var subQ1=sQuery(id+"F12.wireOp",EDGE,"E77.0.2.1");var subQ2=makeQuery(id+"F12.imprint","INTERSECT",VERTEX,{"derivedFrom":[subQ1,subQ0]});Q31=makeQuery(id+"F12.imprint","IMPRINT",FACE,{"disambiguationData":[TD([[makeQuery(id+"F12.imprint","IMPRINT",EDGE,{"disambiguationData":[TD([[subQ2,-1.0]])],"derivedFrom":subQ1}),-1.0]])]});}
            var Q32;
            {var subQ0=sQuery(id+"F12.wireOp",EDGE,"E77.0.2.13");var subQ1=sQuery(id+"F12.wireOp",EDGE,"E77.0.2.1");var subQ2=makeQuery(id+"F12.imprint","INTERSECT",VERTEX,{"derivedFrom":[subQ1,subQ0]});Q32=makeQuery(id+"F12.imprint","IMPRINT",FACE,{"disambiguationData":[TD([[makeQuery(id+"F12.imprint","IMPRINT",EDGE,{"disambiguationData":[TD([[subQ2,-1.0]])],"derivedFrom":subQ1}),1.0]])]});}
            var Q33;
            {var subQ0=sQuery(id+"F12.wireOp",EDGE,"E77.0.2.13");var subQ1=sQuery(id+"F12.wireOp",EDGE,"E77.0.2.5");var subQ2=makeQuery(id+"F12.imprint","INTERSECT",VERTEX,{"derivedFrom":[subQ1,subQ0]});Q33=makeQuery(id+"F12.imprint","IMPRINT",FACE,{"disambiguationData":[TD([[makeQuery(id+"F12.imprint","IMPRINT",EDGE,{"disambiguationData":[TD([[subQ2,1.0]])],"derivedFrom":subQ1}),1.0]])]});}
            var Q34;
            {var subQ0=sQuery(id+"F12.wireOp",EDGE,"E77.0.2.13");var subQ1=sQuery(id+"F12.wireOp",EDGE,"E77.0.2.5");var subQ2=makeQuery(id+"F12.imprint","INTERSECT",VERTEX,{"derivedFrom":[subQ1,subQ0]});Q34=makeQuery(id+"F12.imprint","IMPRINT",FACE,{"disambiguationData":[TD([[makeQuery(id+"F12.imprint","IMPRINT",EDGE,{"disambiguationData":[TD([[subQ2,-1.0]])],"derivedFrom":subQ1}),1.0]])]});}
            var Q35;
            {var subQ0=sQuery(id+"F12.wireOp",EDGE,"E77.0.2.14");var subQ1=sQuery(id+"F12.wireOp",EDGE,"E77.0.2.4");var subQ2=makeQuery(id+"F12.imprint","INTERSECT",VERTEX,{"derivedFrom":[subQ1,subQ0]});Q35=makeQuery(id+"F12.imprint","IMPRINT",FACE,{"disambiguationData":[TD([[makeQuery(id+"F12.imprint","IMPRINT",EDGE,{"disambiguationData":[TD([[subQ2,-1.0]])],"derivedFrom":subQ1}),1.0]])]});}
            var Q36;
            {var subQ0=sQuery(id+"F12.wireOp",EDGE,"E77.0.2.14");var subQ1=sQuery(id+"F12.wireOp",EDGE,"E77.0.2.4");var subQ2=makeQuery(id+"F12.imprint","INTERSECT",VERTEX,{"derivedFrom":[subQ1,subQ0]});Q36=makeQuery(id+"F12.imprint","IMPRINT",FACE,{"disambiguationData":[TD([[makeQuery(id+"F12.imprint","IMPRINT",EDGE,{"disambiguationData":[TD([[subQ2,1.0]])],"derivedFrom":subQ1}),1.0]])]});}
            var Q37;
            Q37=makeQuery(id+"F12.imprint","IMPRINT",FACE,{"disambiguationData":[TD([[makeQuery(id+"F12.imprint","IMPRINT",EDGE,{"derivedFrom":sQuery(id+"F12.wireOp",EDGE,"E77.0.2.3")}),1.0]])]});
            var Q38;
            {var subQ0=sQuery(id+"F12.wireOp",EDGE,"E77.0.1.9");var subQ1=sQuery(id+"F12.wireOp",EDGE,"E77.0.1.8");var subQ2=makeQuery(id+"F12.imprint","INTERSECT",VERTEX,{"derivedFrom":[subQ1,subQ0]});Q38=makeQuery(id+"F12.imprint","IMPRINT",FACE,{"disambiguationData":[TD([[makeQuery(id+"F12.imprint","IMPRINT",EDGE,{"disambiguationData":[TD([[subQ2,1.0]])],"derivedFrom":subQ1}),1.0]])]});}
            var Q39;
            {var subQ0=sQuery(id+"F12.wireOp",EDGE,"E77.0.1.13");var subQ1=sQuery(id+"F12.wireOp",EDGE,"E77.0.1.1");var subQ2=makeQuery(id+"F12.imprint","INTERSECT",VERTEX,{"derivedFrom":[subQ1,subQ0]});Q39=makeQuery(id+"F12.imprint","IMPRINT",FACE,{"disambiguationData":[TD([[makeQuery(id+"F12.imprint","IMPRINT",EDGE,{"disambiguationData":[TD([[subQ2,-1.0]])],"derivedFrom":subQ1}),1.0]])]});}
            extrude(context, id + "F13", {"entities" : qUnion([Q0, Q1, Q2, Q3, Q4, Q5, Q6, Q7, Q8, Q9, Q10, Q11, Q12, Q13, Q14, Q15, Q16, Q17, Q18, Q19, Q20, Q21, Q22, Q23, Q24, Q25, Q26, Q27, Q28, Q29, Q30, Q31, Q32, Q33, Q34, Q35, Q36, Q37, Q38, Q39]), "operationType" : NewBodyOperationType.REMOVE, "oppositeDirection" : true, "depth" : 4 * mm});
        }
        {
            var Q0;
            {var subQ0=sQuery(id+"F0.wireOp",EDGE,"E0.left");var subQ2=sQuery(id+"F2.wireOp",EDGE,"E2.top");var subQ3=sQuery(id+"F0.wireOp",EDGE,"E0.top");Q0=makeQuery(id+"F5.boolean.opBoolean","SPLIT",FACE,{"disambiguationData":[TD([makeQuery(id+"F1.opExtrude","SWEPT_FACE",FACE,{"disambiguationData":[OSD([subQ0])]})])],"derivedFrom":makeQuery(id+"F3.boolean.opBoolean","MERGE",FACE,{"derivedFrom":[makeQuery(id+"F1.opExtrude","SWEPT_FACE",FACE,{"disambiguationData":[OSD([subQ3])]}),makeQuery(id+"F3.opExtrude","SWEPT_FACE",FACE,{"disambiguationData":[OSD([subQ2])]})]})});}
            var sketch = newSketch(context, id + "F14", { "sketchPlane" : qUnion([Q0])});
            skLineSegment(sketch, "E79", {"start": v(-24.75, 3) * mm, "end": v(-21.75, 3) * mm});
            skLineSegment(sketch, "E80", {"start": v(-13.75, 3) * mm, "end": v(-16.75, 3) * mm});
            skLineSegment(sketch, "E81", {"start": v(-21.75, 3) * mm, "end": v(-16.75, 3) * mm});
            skLineSegment(sketch, "E82", {"start": v(-16.75, 3) * mm, "end": v(-19.25, 7.33) * mm});
            skLineSegment(sketch, "E83", {"start": v(-19.25, 7.33) * mm, "end": v(-21.75, 3) * mm});
            skLineSegment(sketch, "E84", {"start": v(-19.25, 3) * mm, "end": v(-19.25, 0) * mm});
            skLineSegment(sketch, "E85.0.1.0", {"start": v(-19.25, 14.66) * mm, "end": v(-21.75, 10.33) * mm});
            skLineSegment(sketch, "E85.0.1.1", {"start": v(-16.75, 10.33) * mm, "end": v(-19.25, 14.66) * mm});
            skLineSegment(sketch, "E85.0.1.2", {"start": v(-24.75, 10.33) * mm, "end": v(-21.75, 10.33) * mm});
            skLineSegment(sketch, "E85.0.1.3", {"start": v(-21.75, 10.33) * mm, "end": v(-16.75, 10.33) * mm});
            skLineSegment(sketch, "E85.0.1.4", {"start": v(-13.75, 10.33) * mm, "end": v(-16.75, 10.33) * mm});
            skLineSegment(sketch, "E85.0.1.5", {"start": v(-19.25, 10.33) * mm, "end": v(-19.25, 7.33) * mm});
            skLineSegment(sketch, "E85.0.2.0", {"start": v(-19.25, 22) * mm, "end": v(-21.75, 17.66) * mm});
            skLineSegment(sketch, "E85.0.2.1", {"start": v(-16.75, 17.66) * mm, "end": v(-19.25, 22) * mm});
            skLineSegment(sketch, "E85.0.2.2", {"start": v(-24.75, 17.66) * mm, "end": v(-21.75, 17.66) * mm});
            skLineSegment(sketch, "E85.0.2.3", {"start": v(-21.75, 17.66) * mm, "end": v(-16.75, 17.66) * mm});
            skLineSegment(sketch, "E85.0.2.4", {"start": v(-13.75, 17.66) * mm, "end": v(-16.75, 17.66) * mm});
            skLineSegment(sketch, "E85.0.2.5", {"start": v(-19.25, 17.66) * mm, "end": v(-19.25, 14.66) * mm});
            skLineSegment(sketch, "E85.0.3.0", {"start": v(-19.25, 29.32) * mm, "end": v(-21.75, 25) * mm});
            skLineSegment(sketch, "E85.0.3.1", {"start": v(-16.75, 25) * mm, "end": v(-19.25, 29.32) * mm});
            skLineSegment(sketch, "E85.0.3.2", {"start": v(-24.75, 25) * mm, "end": v(-21.75, 25) * mm});
            skLineSegment(sketch, "E85.0.3.3", {"start": v(-21.75, 25) * mm, "end": v(-16.75, 25) * mm});
            skLineSegment(sketch, "E85.0.3.4", {"start": v(-13.75, 25) * mm, "end": v(-16.75, 25) * mm});
            skLineSegment(sketch, "E85.0.3.5", {"start": v(-19.25, 25) * mm, "end": v(-19.25, 22) * mm});
            skLineSegment(sketch, "E85.0.4.0", {"start": v(-19.25, 36.65) * mm, "end": v(-21.75, 32.32) * mm});
            skLineSegment(sketch, "E85.0.4.1", {"start": v(-16.75, 32.32) * mm, "end": v(-19.25, 36.65) * mm});
            skLineSegment(sketch, "E85.0.4.2", {"start": v(-24.75, 32.32) * mm, "end": v(-21.75, 32.32) * mm});
            skLineSegment(sketch, "E85.0.4.3", {"start": v(-21.75, 32.32) * mm, "end": v(-16.75, 32.32) * mm});
            skLineSegment(sketch, "E85.0.4.4", {"start": v(-13.75, 32.32) * mm, "end": v(-16.75, 32.32) * mm});
            skLineSegment(sketch, "E85.0.4.5", {"start": v(-19.25, 32.32) * mm, "end": v(-19.25, 29.32) * mm});
            skLineSegment(sketch, "E85.0.5.0", {"start": v(-19.25, 43.98) * mm, "end": v(-21.75, 39.65) * mm});
            skLineSegment(sketch, "E85.0.5.1", {"start": v(-16.75, 39.65) * mm, "end": v(-19.25, 43.98) * mm});
            skLineSegment(sketch, "E85.0.5.2", {"start": v(-24.75, 39.65) * mm, "end": v(-21.75, 39.65) * mm});
            skLineSegment(sketch, "E85.0.5.3", {"start": v(-21.75, 39.65) * mm, "end": v(-16.75, 39.65) * mm});
            skLineSegment(sketch, "E85.0.5.4", {"start": v(-13.75, 39.65) * mm, "end": v(-16.75, 39.65) * mm});
            skLineSegment(sketch, "E85.0.5.5", {"start": v(-19.25, 39.65) * mm, "end": v(-19.25, 36.65) * mm});
            skLineSegment(sketch, "E85.0.6.0", {"start": v(-19.25, 51.31) * mm, "end": v(-21.75, 46.98) * mm});
            skLineSegment(sketch, "E85.0.6.1", {"start": v(-16.75, 46.98) * mm, "end": v(-19.25, 51.31) * mm});
            skLineSegment(sketch, "E85.0.6.2", {"start": v(-24.75, 46.98) * mm, "end": v(-21.75, 46.98) * mm});
            skLineSegment(sketch, "E85.0.6.3", {"start": v(-21.75, 46.98) * mm, "end": v(-16.75, 46.98) * mm});
            skLineSegment(sketch, "E85.0.6.4", {"start": v(-13.75, 46.98) * mm, "end": v(-16.75, 46.98) * mm});
            skLineSegment(sketch, "E85.0.6.5", {"start": v(-19.25, 46.98) * mm, "end": v(-19.25, 43.98) * mm});
            skLineSegment(sketch, "E85.0.7.0", {"start": v(-19.25, 58.64) * mm, "end": v(-21.75, 54.31) * mm});
            skLineSegment(sketch, "E85.0.7.1", {"start": v(-16.75, 54.31) * mm, "end": v(-19.25, 58.64) * mm});
            skLineSegment(sketch, "E85.0.7.2", {"start": v(-24.75, 54.31) * mm, "end": v(-21.75, 54.31) * mm});
            skLineSegment(sketch, "E85.0.7.3", {"start": v(-21.75, 54.31) * mm, "end": v(-16.75, 54.31) * mm});
            skLineSegment(sketch, "E85.0.7.4", {"start": v(-13.75, 54.31) * mm, "end": v(-16.75, 54.31) * mm});
            skLineSegment(sketch, "E85.0.7.5", {"start": v(-19.25, 54.31) * mm, "end": v(-19.25, 51.31) * mm});
            skLineSegment(sketch, "E85.0.8.0", {"start": v(-19.25, 65.97) * mm, "end": v(-21.75, 61.64) * mm});
            skLineSegment(sketch, "E85.0.8.1", {"start": v(-16.75, 61.64) * mm, "end": v(-19.25, 65.97) * mm});
            skLineSegment(sketch, "E85.0.8.2", {"start": v(-24.75, 61.64) * mm, "end": v(-21.75, 61.64) * mm});
            skLineSegment(sketch, "E85.0.8.3", {"start": v(-21.75, 61.64) * mm, "end": v(-16.75, 61.64) * mm});
            skLineSegment(sketch, "E85.0.8.4", {"start": v(-13.75, 61.64) * mm, "end": v(-16.75, 61.64) * mm});
            skLineSegment(sketch, "E85.0.8.5", {"start": v(-19.25, 61.64) * mm, "end": v(-19.25, 58.64) * mm});
            skLineSegment(sketch, "E85.0.9.0", {"start": v(-19.25, 73.3) * mm, "end": v(-21.75, 68.97) * mm});
            skLineSegment(sketch, "E85.0.9.1", {"start": v(-16.75, 68.97) * mm, "end": v(-19.25, 73.3) * mm});
            skLineSegment(sketch, "E85.0.9.2", {"start": v(-24.75, 68.97) * mm, "end": v(-21.75, 68.97) * mm});
            skLineSegment(sketch, "E85.0.9.3", {"start": v(-21.75, 68.97) * mm, "end": v(-16.75, 68.97) * mm});
            skLineSegment(sketch, "E85.0.9.4", {"start": v(-13.75, 68.97) * mm, "end": v(-16.75, 68.97) * mm});
            skLineSegment(sketch, "E85.0.9.5", {"start": v(-19.25, 68.97) * mm, "end": v(-19.25, 65.97) * mm});
            skLineSegment(sketch, "E85.0.10.0", {"start": v(-19.25, 80.63) * mm, "end": v(-21.75, 76.3) * mm});
            skLineSegment(sketch, "E85.0.10.1", {"start": v(-16.75, 76.3) * mm, "end": v(-19.25, 80.63) * mm});
            skLineSegment(sketch, "E85.0.10.2", {"start": v(-24.75, 76.3) * mm, "end": v(-21.75, 76.3) * mm});
            skLineSegment(sketch, "E85.0.10.3", {"start": v(-21.75, 76.3) * mm, "end": v(-16.75, 76.3) * mm});
            skLineSegment(sketch, "E85.0.10.4", {"start": v(-13.75, 76.3) * mm, "end": v(-16.75, 76.3) * mm});
            skLineSegment(sketch, "E85.0.10.5", {"start": v(-19.25, 76.3) * mm, "end": v(-19.25, 73.3) * mm});
            skLineSegment(sketch, "E85.0.11.0", {"start": v(-19.25, 87.96) * mm, "end": v(-21.75, 83.63) * mm});
            skLineSegment(sketch, "E85.0.11.1", {"start": v(-16.75, 83.63) * mm, "end": v(-19.25, 87.96) * mm});
            skLineSegment(sketch, "E85.0.11.2", {"start": v(-24.75, 83.63) * mm, "end": v(-21.75, 83.63) * mm});
            skLineSegment(sketch, "E85.0.11.3", {"start": v(-21.75, 83.63) * mm, "end": v(-16.75, 83.63) * mm});
            skLineSegment(sketch, "E85.0.11.4", {"start": v(-13.75, 83.63) * mm, "end": v(-16.75, 83.63) * mm});
            skLineSegment(sketch, "E85.0.11.5", {"start": v(-19.25, 83.63) * mm, "end": v(-19.25, 80.63) * mm});
            skLineSegment(sketch, "E85.0.12.0", {"start": v(-19.25, 95.3) * mm, "end": v(-21.75, 90.96) * mm});
            skLineSegment(sketch, "E85.0.12.1", {"start": v(-16.75, 90.96) * mm, "end": v(-19.25, 95.3) * mm});
            skLineSegment(sketch, "E85.0.12.2", {"start": v(-24.75, 90.96) * mm, "end": v(-21.75, 90.96) * mm});
            skLineSegment(sketch, "E85.0.12.3", {"start": v(-21.75, 90.96) * mm, "end": v(-16.75, 90.96) * mm});
            skLineSegment(sketch, "E85.0.12.4", {"start": v(-13.75, 90.96) * mm, "end": v(-16.75, 90.96) * mm});
            skLineSegment(sketch, "E85.0.12.5", {"start": v(-19.25, 90.96) * mm, "end": v(-19.25, 87.96) * mm});
            skLineSegment(sketch, "E85.0.13.0", {"start": v(-19.25, 102.62) * mm, "end": v(-21.75, 98.3) * mm});
            skLineSegment(sketch, "E85.0.13.1", {"start": v(-16.75, 98.3) * mm, "end": v(-19.25, 102.62) * mm});
            skLineSegment(sketch, "E85.0.13.2", {"start": v(-24.75, 98.3) * mm, "end": v(-21.75, 98.3) * mm});
            skLineSegment(sketch, "E85.0.13.3", {"start": v(-21.75, 98.3) * mm, "end": v(-16.75, 98.3) * mm});
            skLineSegment(sketch, "E85.0.13.4", {"start": v(-13.75, 98.3) * mm, "end": v(-16.75, 98.3) * mm});
            skLineSegment(sketch, "E85.0.13.5", {"start": v(-19.25, 98.3) * mm, "end": v(-19.25, 95.3) * mm});
            skLineSegment(sketch, "E85.0.14.0", {"start": v(-19.25, 109.95) * mm, "end": v(-21.75, 105.62) * mm});
            skLineSegment(sketch, "E85.0.14.1", {"start": v(-16.75, 105.62) * mm, "end": v(-19.25, 109.95) * mm});
            skLineSegment(sketch, "E85.0.14.2", {"start": v(-24.75, 105.62) * mm, "end": v(-21.75, 105.62) * mm});
            skLineSegment(sketch, "E85.0.14.3", {"start": v(-21.75, 105.62) * mm, "end": v(-16.75, 105.62) * mm});
            skLineSegment(sketch, "E85.0.14.4", {"start": v(-13.75, 105.62) * mm, "end": v(-16.75, 105.62) * mm});
            skLineSegment(sketch, "E85.0.14.5", {"start": v(-19.25, 105.62) * mm, "end": v(-19.25, 102.62) * mm});
            skLineSegment(sketch, "E85.direction1", {"start": v(-24.75, 3) * mm, "end": v(13.75, 3) * mm, "construction": true});
            skLineSegment(sketch, "E85.direction2", {"start": v(-24.75, 3) * mm, "end": v(-24.75, 10.33) * mm, "construction": true});
            skLineSegment(sketch, "E86.0.1.0", {"start": v(19.25, 7.33) * mm, "end": v(16.75, 3) * mm});
            skLineSegment(sketch, "E86.3.1.0", {"start": v(21.75, 3) * mm, "end": v(19.25, 7.33) * mm});
            skLineSegment(sketch, "E86.6.1.0", {"start": v(13.75, 3) * mm, "end": v(16.75, 3) * mm});
            skLineSegment(sketch, "E86.9.1.0", {"start": v(16.75, 3) * mm, "end": v(21.75, 3) * mm});
            skLineSegment(sketch, "E86.12.1.0", {"start": v(24.75, 3) * mm, "end": v(21.75, 3) * mm});
            skLineSegment(sketch, "E86.15.1.0", {"start": v(19.25, 3) * mm, "end": v(19.25, 0) * mm});
            skLineSegment(sketch, "E86.0.1.1", {"start": v(19.25, 14.66) * mm, "end": v(16.75, 10.33) * mm});
            skLineSegment(sketch, "E86.3.1.1", {"start": v(21.75, 10.33) * mm, "end": v(19.25, 14.66) * mm});
            skLineSegment(sketch, "E86.6.1.1", {"start": v(13.75, 10.33) * mm, "end": v(16.75, 10.33) * mm});
            skLineSegment(sketch, "E86.9.1.1", {"start": v(16.75, 10.33) * mm, "end": v(21.75, 10.33) * mm});
            skLineSegment(sketch, "E86.12.1.1", {"start": v(24.75, 10.33) * mm, "end": v(21.75, 10.33) * mm});
            skLineSegment(sketch, "E86.15.1.1", {"start": v(19.25, 10.33) * mm, "end": v(19.25, 7.33) * mm});
            skLineSegment(sketch, "E86.0.1.2", {"start": v(19.25, 22) * mm, "end": v(16.75, 17.66) * mm});
            skLineSegment(sketch, "E86.3.1.2", {"start": v(21.75, 17.66) * mm, "end": v(19.25, 22) * mm});
            skLineSegment(sketch, "E86.6.1.2", {"start": v(13.75, 17.66) * mm, "end": v(16.75, 17.66) * mm});
            skLineSegment(sketch, "E86.9.1.2", {"start": v(16.75, 17.66) * mm, "end": v(21.75, 17.66) * mm});
            skLineSegment(sketch, "E86.12.1.2", {"start": v(24.75, 17.66) * mm, "end": v(21.75, 17.66) * mm});
            skLineSegment(sketch, "E86.15.1.2", {"start": v(19.25, 17.66) * mm, "end": v(19.25, 14.66) * mm});
            skLineSegment(sketch, "E86.0.1.3", {"start": v(19.25, 29.32) * mm, "end": v(16.75, 24.99) * mm});
            skLineSegment(sketch, "E86.3.1.3", {"start": v(21.75, 24.99) * mm, "end": v(19.25, 29.32) * mm});
            skLineSegment(sketch, "E86.6.1.3", {"start": v(13.75, 25) * mm, "end": v(16.75, 25) * mm});
            skLineSegment(sketch, "E86.9.1.3", {"start": v(16.75, 25) * mm, "end": v(21.75, 25) * mm});
            skLineSegment(sketch, "E86.12.1.3", {"start": v(24.75, 25) * mm, "end": v(21.75, 25) * mm});
            skLineSegment(sketch, "E86.15.1.3", {"start": v(19.25, 25) * mm, "end": v(19.25, 22) * mm});
            skLineSegment(sketch, "E86.0.1.4", {"start": v(19.25, 36.65) * mm, "end": v(16.75, 32.32) * mm});
            skLineSegment(sketch, "E86.3.1.4", {"start": v(21.75, 32.32) * mm, "end": v(19.25, 36.65) * mm});
            skLineSegment(sketch, "E86.6.1.4", {"start": v(13.75, 32.32) * mm, "end": v(16.75, 32.32) * mm});
            skLineSegment(sketch, "E86.9.1.4", {"start": v(16.75, 32.32) * mm, "end": v(21.75, 32.32) * mm});
            skLineSegment(sketch, "E86.12.1.4", {"start": v(24.75, 32.32) * mm, "end": v(21.75, 32.32) * mm});
            skLineSegment(sketch, "E86.15.1.4", {"start": v(19.25, 32.32) * mm, "end": v(19.25, 29.32) * mm});
            skLineSegment(sketch, "E86.0.1.5", {"start": v(19.25, 43.98) * mm, "end": v(16.75, 39.65) * mm});
            skLineSegment(sketch, "E86.3.1.5", {"start": v(21.75, 39.65) * mm, "end": v(19.25, 43.98) * mm});
            skLineSegment(sketch, "E86.6.1.5", {"start": v(13.75, 39.65) * mm, "end": v(16.75, 39.65) * mm});
            skLineSegment(sketch, "E86.9.1.5", {"start": v(16.75, 39.65) * mm, "end": v(21.75, 39.65) * mm});
            skLineSegment(sketch, "E86.12.1.5", {"start": v(24.75, 39.65) * mm, "end": v(21.75, 39.65) * mm});
            skLineSegment(sketch, "E86.15.1.5", {"start": v(19.25, 39.65) * mm, "end": v(19.25, 36.65) * mm});
            skLineSegment(sketch, "E86.0.1.6", {"start": v(19.25, 51.31) * mm, "end": v(16.75, 46.98) * mm});
            skLineSegment(sketch, "E86.3.1.6", {"start": v(21.75, 46.98) * mm, "end": v(19.25, 51.31) * mm});
            skLineSegment(sketch, "E86.6.1.6", {"start": v(13.75, 46.98) * mm, "end": v(16.75, 46.98) * mm});
            skLineSegment(sketch, "E86.9.1.6", {"start": v(16.75, 46.98) * mm, "end": v(21.75, 46.98) * mm});
            skLineSegment(sketch, "E86.12.1.6", {"start": v(24.75, 46.98) * mm, "end": v(21.75, 46.98) * mm});
            skLineSegment(sketch, "E86.15.1.6", {"start": v(19.25, 46.98) * mm, "end": v(19.25, 43.98) * mm});
            skLineSegment(sketch, "E86.0.1.7", {"start": v(19.25, 58.64) * mm, "end": v(16.75, 54.31) * mm});
            skLineSegment(sketch, "E86.3.1.7", {"start": v(21.75, 54.31) * mm, "end": v(19.25, 58.64) * mm});
            skLineSegment(sketch, "E86.6.1.7", {"start": v(13.75, 54.31) * mm, "end": v(16.75, 54.31) * mm});
            skLineSegment(sketch, "E86.9.1.7", {"start": v(16.75, 54.31) * mm, "end": v(21.75, 54.31) * mm});
            skLineSegment(sketch, "E86.12.1.7", {"start": v(24.75, 54.31) * mm, "end": v(21.75, 54.31) * mm});
            skLineSegment(sketch, "E86.15.1.7", {"start": v(19.25, 54.31) * mm, "end": v(19.25, 51.31) * mm});
            skLineSegment(sketch, "E86.0.1.8", {"start": v(19.25, 65.97) * mm, "end": v(16.75, 61.64) * mm});
            skLineSegment(sketch, "E86.3.1.8", {"start": v(21.75, 61.64) * mm, "end": v(19.25, 65.97) * mm});
            skLineSegment(sketch, "E86.6.1.8", {"start": v(13.75, 61.64) * mm, "end": v(16.75, 61.64) * mm});
            skLineSegment(sketch, "E86.9.1.8", {"start": v(16.75, 61.64) * mm, "end": v(21.75, 61.64) * mm});
            skLineSegment(sketch, "E86.12.1.8", {"start": v(24.75, 61.64) * mm, "end": v(21.75, 61.64) * mm});
            skLineSegment(sketch, "E86.15.1.8", {"start": v(19.25, 61.64) * mm, "end": v(19.25, 58.64) * mm});
            skLineSegment(sketch, "E86.0.1.9", {"start": v(19.25, 73.3) * mm, "end": v(16.75, 68.97) * mm});
            skLineSegment(sketch, "E86.3.1.9", {"start": v(21.75, 68.97) * mm, "end": v(19.25, 73.3) * mm});
            skLineSegment(sketch, "E86.6.1.9", {"start": v(13.75, 68.97) * mm, "end": v(16.75, 68.97) * mm});
            skLineSegment(sketch, "E86.9.1.9", {"start": v(16.75, 68.97) * mm, "end": v(21.75, 68.97) * mm});
            skLineSegment(sketch, "E86.12.1.9", {"start": v(24.75, 68.97) * mm, "end": v(21.75, 68.97) * mm});
            skLineSegment(sketch, "E86.15.1.9", {"start": v(19.25, 68.97) * mm, "end": v(19.25, 65.97) * mm});
            skLineSegment(sketch, "E86.0.1.10", {"start": v(19.25, 80.63) * mm, "end": v(16.75, 76.3) * mm});
            skLineSegment(sketch, "E86.3.1.10", {"start": v(21.75, 76.3) * mm, "end": v(19.25, 80.63) * mm});
            skLineSegment(sketch, "E86.6.1.10", {"start": v(13.75, 76.3) * mm, "end": v(16.75, 76.3) * mm});
            skLineSegment(sketch, "E86.9.1.10", {"start": v(16.75, 76.3) * mm, "end": v(21.75, 76.3) * mm});
            skLineSegment(sketch, "E86.12.1.10", {"start": v(24.75, 76.3) * mm, "end": v(21.75, 76.3) * mm});
            skLineSegment(sketch, "E86.15.1.10", {"start": v(19.25, 76.3) * mm, "end": v(19.25, 73.3) * mm});
            skLineSegment(sketch, "E86.0.1.11", {"start": v(19.25, 87.96) * mm, "end": v(16.75, 83.63) * mm});
            skLineSegment(sketch, "E86.3.1.11", {"start": v(21.75, 83.63) * mm, "end": v(19.25, 87.96) * mm});
            skLineSegment(sketch, "E86.6.1.11", {"start": v(13.75, 83.63) * mm, "end": v(16.75, 83.63) * mm});
            skLineSegment(sketch, "E86.9.1.11", {"start": v(16.75, 83.63) * mm, "end": v(21.75, 83.63) * mm});
            skLineSegment(sketch, "E86.12.1.11", {"start": v(24.75, 83.63) * mm, "end": v(21.75, 83.63) * mm});
            skLineSegment(sketch, "E86.15.1.11", {"start": v(19.25, 83.63) * mm, "end": v(19.25, 80.63) * mm});
            skLineSegment(sketch, "E86.0.1.12", {"start": v(19.25, 95.3) * mm, "end": v(16.75, 90.96) * mm});
            skLineSegment(sketch, "E86.3.1.12", {"start": v(21.75, 90.96) * mm, "end": v(19.25, 95.3) * mm});
            skLineSegment(sketch, "E86.6.1.12", {"start": v(13.75, 90.96) * mm, "end": v(16.75, 90.96) * mm});
            skLineSegment(sketch, "E86.9.1.12", {"start": v(16.75, 90.96) * mm, "end": v(21.75, 90.96) * mm});
            skLineSegment(sketch, "E86.12.1.12", {"start": v(24.75, 90.96) * mm, "end": v(21.75, 90.96) * mm});
            skLineSegment(sketch, "E86.15.1.12", {"start": v(19.25, 90.96) * mm, "end": v(19.25, 87.96) * mm});
            skLineSegment(sketch, "E86.0.1.13", {"start": v(19.25, 102.62) * mm, "end": v(16.75, 98.3) * mm});
            skLineSegment(sketch, "E86.3.1.13", {"start": v(21.75, 98.3) * mm, "end": v(19.25, 102.62) * mm});
            skLineSegment(sketch, "E86.6.1.13", {"start": v(13.75, 98.3) * mm, "end": v(16.75, 98.3) * mm});
            skLineSegment(sketch, "E86.9.1.13", {"start": v(16.75, 98.3) * mm, "end": v(21.75, 98.3) * mm});
            skLineSegment(sketch, "E86.12.1.13", {"start": v(24.75, 98.3) * mm, "end": v(21.75, 98.3) * mm});
            skLineSegment(sketch, "E86.15.1.13", {"start": v(19.25, 98.3) * mm, "end": v(19.25, 95.3) * mm});
            skLineSegment(sketch, "E86.0.1.14", {"start": v(19.25, 109.95) * mm, "end": v(16.75, 105.62) * mm});
            skLineSegment(sketch, "E86.3.1.14", {"start": v(21.75, 105.62) * mm, "end": v(19.25, 109.95) * mm});
            skLineSegment(sketch, "E86.6.1.14", {"start": v(13.75, 105.62) * mm, "end": v(16.75, 105.62) * mm});
            skLineSegment(sketch, "E86.9.1.14", {"start": v(16.75, 105.62) * mm, "end": v(21.75, 105.62) * mm});
            skLineSegment(sketch, "E86.12.1.14", {"start": v(24.75, 105.62) * mm, "end": v(21.75, 105.62) * mm});
            skLineSegment(sketch, "E86.15.1.14", {"start": v(19.25, 105.62) * mm, "end": v(19.25, 102.62) * mm});
            skLineSegment(sketch, "E87", {"start": v(-19.25, 7.33) * mm, "end": v(-24.75, 7.33) * mm});
            skSolve(sketch);
        }
        {
            var Q0;
            {var subQ0=sQuery(id+"F14.wireOp",EDGE,"E85.0.14.0");Q0=makeQuery(id+"F14.imprint","IMPRINT",FACE,{"disambiguationData":[TD([[makeQuery(id+"F14.imprint","IMPRINT",EDGE,{"derivedFrom":subQ0}),1.0]])]});}
            var Q1;
            {var subQ0=sQuery(id+"F14.wireOp",EDGE,"E85.0.13.0");Q1=makeQuery(id+"F14.imprint","IMPRINT",FACE,{"disambiguationData":[TD([[makeQuery(id+"F14.imprint","IMPRINT",EDGE,{"derivedFrom":subQ0}),1.0]])]});}
            var Q2;
            {var subQ0=sQuery(id+"F14.wireOp",EDGE,"E85.0.12.0");Q2=makeQuery(id+"F14.imprint","IMPRINT",FACE,{"disambiguationData":[TD([[makeQuery(id+"F14.imprint","IMPRINT",EDGE,{"derivedFrom":subQ0}),1.0]])]});}
            var Q3;
            {var subQ0=sQuery(id+"F14.wireOp",EDGE,"E85.0.11.0");Q3=makeQuery(id+"F14.imprint","IMPRINT",FACE,{"disambiguationData":[TD([[makeQuery(id+"F14.imprint","IMPRINT",EDGE,{"derivedFrom":subQ0}),1.0]])]});}
            var Q4;
            {var subQ0=sQuery(id+"F14.wireOp",EDGE,"E85.0.10.0");Q4=makeQuery(id+"F14.imprint","IMPRINT",FACE,{"disambiguationData":[TD([[makeQuery(id+"F14.imprint","IMPRINT",EDGE,{"derivedFrom":subQ0}),1.0]])]});}
            var Q5;
            {var subQ0=sQuery(id+"F14.wireOp",EDGE,"E85.0.9.0");Q5=makeQuery(id+"F14.imprint","IMPRINT",FACE,{"disambiguationData":[TD([[makeQuery(id+"F14.imprint","IMPRINT",EDGE,{"derivedFrom":subQ0}),1.0]])]});}
            var Q6;
            {var subQ0=sQuery(id+"F14.wireOp",EDGE,"E85.0.8.0");Q6=makeQuery(id+"F14.imprint","IMPRINT",FACE,{"disambiguationData":[TD([[makeQuery(id+"F14.imprint","IMPRINT",EDGE,{"derivedFrom":subQ0}),1.0]])]});}
            var Q7;
            {var subQ0=sQuery(id+"F14.wireOp",EDGE,"E85.0.7.0");Q7=makeQuery(id+"F14.imprint","IMPRINT",FACE,{"disambiguationData":[TD([[makeQuery(id+"F14.imprint","IMPRINT",EDGE,{"derivedFrom":subQ0}),1.0]])]});}
            var Q8;
            {var subQ0=sQuery(id+"F14.wireOp",EDGE,"E85.0.6.0");Q8=makeQuery(id+"F14.imprint","IMPRINT",FACE,{"disambiguationData":[TD([[makeQuery(id+"F14.imprint","IMPRINT",EDGE,{"derivedFrom":subQ0}),1.0]])]});}
            var Q9;
            {var subQ0=sQuery(id+"F14.wireOp",EDGE,"E85.0.5.0");Q9=makeQuery(id+"F14.imprint","IMPRINT",FACE,{"disambiguationData":[TD([[makeQuery(id+"F14.imprint","IMPRINT",EDGE,{"derivedFrom":subQ0}),1.0]])]});}
            var Q10;
            {var subQ0=sQuery(id+"F14.wireOp",EDGE,"E85.0.4.0");Q10=makeQuery(id+"F14.imprint","IMPRINT",FACE,{"disambiguationData":[TD([[makeQuery(id+"F14.imprint","IMPRINT",EDGE,{"derivedFrom":subQ0}),1.0]])]});}
            var Q11;
            {var subQ0=sQuery(id+"F14.wireOp",EDGE,"E85.0.3.0");Q11=makeQuery(id+"F14.imprint","IMPRINT",FACE,{"disambiguationData":[TD([[makeQuery(id+"F14.imprint","IMPRINT",EDGE,{"derivedFrom":subQ0}),1.0]])]});}
            var Q12;
            {var subQ0=sQuery(id+"F14.wireOp",EDGE,"E85.0.2.0");Q12=makeQuery(id+"F14.imprint","IMPRINT",FACE,{"disambiguationData":[TD([[makeQuery(id+"F14.imprint","IMPRINT",EDGE,{"derivedFrom":subQ0}),1.0]])]});}
            var Q13;
            {var subQ0=sQuery(id+"F14.wireOp",EDGE,"E85.0.1.0");Q13=makeQuery(id+"F14.imprint","IMPRINT",FACE,{"disambiguationData":[TD([[makeQuery(id+"F14.imprint","IMPRINT",EDGE,{"derivedFrom":subQ0}),1.0]])]});}
            var Q14;
            {var subQ3=sQuery(id+"F14.wireOp",EDGE,"E82");Q14=makeQuery(id+"F14.imprint","IMPRINT",FACE,{"disambiguationData":[TD([[makeQuery(id+"F14.imprint","IMPRINT",EDGE,{"derivedFrom":subQ3}),1.0]])]});}
            var Q15;
            {var subQ0=sQuery(id+"F14.wireOp",EDGE,"E86.0.1.0");Q15=makeQuery(id+"F14.imprint","IMPRINT",FACE,{"disambiguationData":[TD([[makeQuery(id+"F14.imprint","IMPRINT",EDGE,{"derivedFrom":subQ0}),1.0]])]});}
            var Q16;
            {var subQ0=sQuery(id+"F14.wireOp",EDGE,"E86.0.1.1");Q16=makeQuery(id+"F14.imprint","IMPRINT",FACE,{"disambiguationData":[TD([[makeQuery(id+"F14.imprint","IMPRINT",EDGE,{"derivedFrom":subQ0}),1.0]])]});}
            var Q17;
            {var subQ0=sQuery(id+"F14.wireOp",EDGE,"E86.0.1.2");Q17=makeQuery(id+"F14.imprint","IMPRINT",FACE,{"disambiguationData":[TD([[makeQuery(id+"F14.imprint","IMPRINT",EDGE,{"derivedFrom":subQ0}),1.0]])]});}
            var Q18;
            {var subQ0=sQuery(id+"F14.wireOp",EDGE,"E86.0.1.3");Q18=makeQuery(id+"F14.imprint","IMPRINT",FACE,{"disambiguationData":[TD([[makeQuery(id+"F14.imprint","IMPRINT",EDGE,{"derivedFrom":subQ0}),1.0]])]});}
            var Q19;
            {var subQ0=sQuery(id+"F14.wireOp",EDGE,"E86.0.1.4");Q19=makeQuery(id+"F14.imprint","IMPRINT",FACE,{"disambiguationData":[TD([[makeQuery(id+"F14.imprint","IMPRINT",EDGE,{"derivedFrom":subQ0}),1.0]])]});}
            var Q20;
            {var subQ0=sQuery(id+"F14.wireOp",EDGE,"E86.0.1.5");Q20=makeQuery(id+"F14.imprint","IMPRINT",FACE,{"disambiguationData":[TD([[makeQuery(id+"F14.imprint","IMPRINT",EDGE,{"derivedFrom":subQ0}),1.0]])]});}
            var Q21;
            {var subQ0=sQuery(id+"F14.wireOp",EDGE,"E86.0.1.6");Q21=makeQuery(id+"F14.imprint","IMPRINT",FACE,{"disambiguationData":[TD([[makeQuery(id+"F14.imprint","IMPRINT",EDGE,{"derivedFrom":subQ0}),1.0]])]});}
            var Q22;
            {var subQ0=sQuery(id+"F14.wireOp",EDGE,"E86.0.1.7");Q22=makeQuery(id+"F14.imprint","IMPRINT",FACE,{"disambiguationData":[TD([[makeQuery(id+"F14.imprint","IMPRINT",EDGE,{"derivedFrom":subQ0}),1.0]])]});}
            var Q23;
            {var subQ0=sQuery(id+"F14.wireOp",EDGE,"E86.0.1.8");Q23=makeQuery(id+"F14.imprint","IMPRINT",FACE,{"disambiguationData":[TD([[makeQuery(id+"F14.imprint","IMPRINT",EDGE,{"derivedFrom":subQ0}),1.0]])]});}
            var Q24;
            {var subQ0=sQuery(id+"F14.wireOp",EDGE,"E86.0.1.9");Q24=makeQuery(id+"F14.imprint","IMPRINT",FACE,{"disambiguationData":[TD([[makeQuery(id+"F14.imprint","IMPRINT",EDGE,{"derivedFrom":subQ0}),1.0]])]});}
            var Q25;
            {var subQ0=sQuery(id+"F14.wireOp",EDGE,"E86.0.1.10");Q25=makeQuery(id+"F14.imprint","IMPRINT",FACE,{"disambiguationData":[TD([[makeQuery(id+"F14.imprint","IMPRINT",EDGE,{"derivedFrom":subQ0}),1.0]])]});}
            var Q26;
            {var subQ0=sQuery(id+"F14.wireOp",EDGE,"E86.0.1.11");Q26=makeQuery(id+"F14.imprint","IMPRINT",FACE,{"disambiguationData":[TD([[makeQuery(id+"F14.imprint","IMPRINT",EDGE,{"derivedFrom":subQ0}),1.0]])]});}
            var Q27;
            {var subQ0=sQuery(id+"F14.wireOp",EDGE,"E86.0.1.12");Q27=makeQuery(id+"F14.imprint","IMPRINT",FACE,{"disambiguationData":[TD([[makeQuery(id+"F14.imprint","IMPRINT",EDGE,{"derivedFrom":subQ0}),1.0]])]});}
            var Q28;
            {var subQ0=sQuery(id+"F14.wireOp",EDGE,"E86.0.1.13");Q28=makeQuery(id+"F14.imprint","IMPRINT",FACE,{"disambiguationData":[TD([[makeQuery(id+"F14.imprint","IMPRINT",EDGE,{"derivedFrom":subQ0}),1.0]])]});}
            var Q29;
            {var subQ0=sQuery(id+"F14.wireOp",EDGE,"E86.0.1.14");Q29=makeQuery(id+"F14.imprint","IMPRINT",FACE,{"disambiguationData":[TD([[makeQuery(id+"F14.imprint","IMPRINT",EDGE,{"derivedFrom":subQ0}),1.0]])]});}
            extrude(context, id + "F15", {"entities" : qUnion([Q0, Q1, Q2, Q3, Q4, Q5, Q6, Q7, Q8, Q9, Q10, Q11, Q12, Q13, Q14, Q15, Q16, Q17, Q18, Q19, Q20, Q21, Q22, Q23, Q24, Q25, Q26, Q27, Q28, Q29]), "operationType" : NewBodyOperationType.REMOVE, "oppositeDirection" : true, "depth" : 25 * mm});
        }
    });
